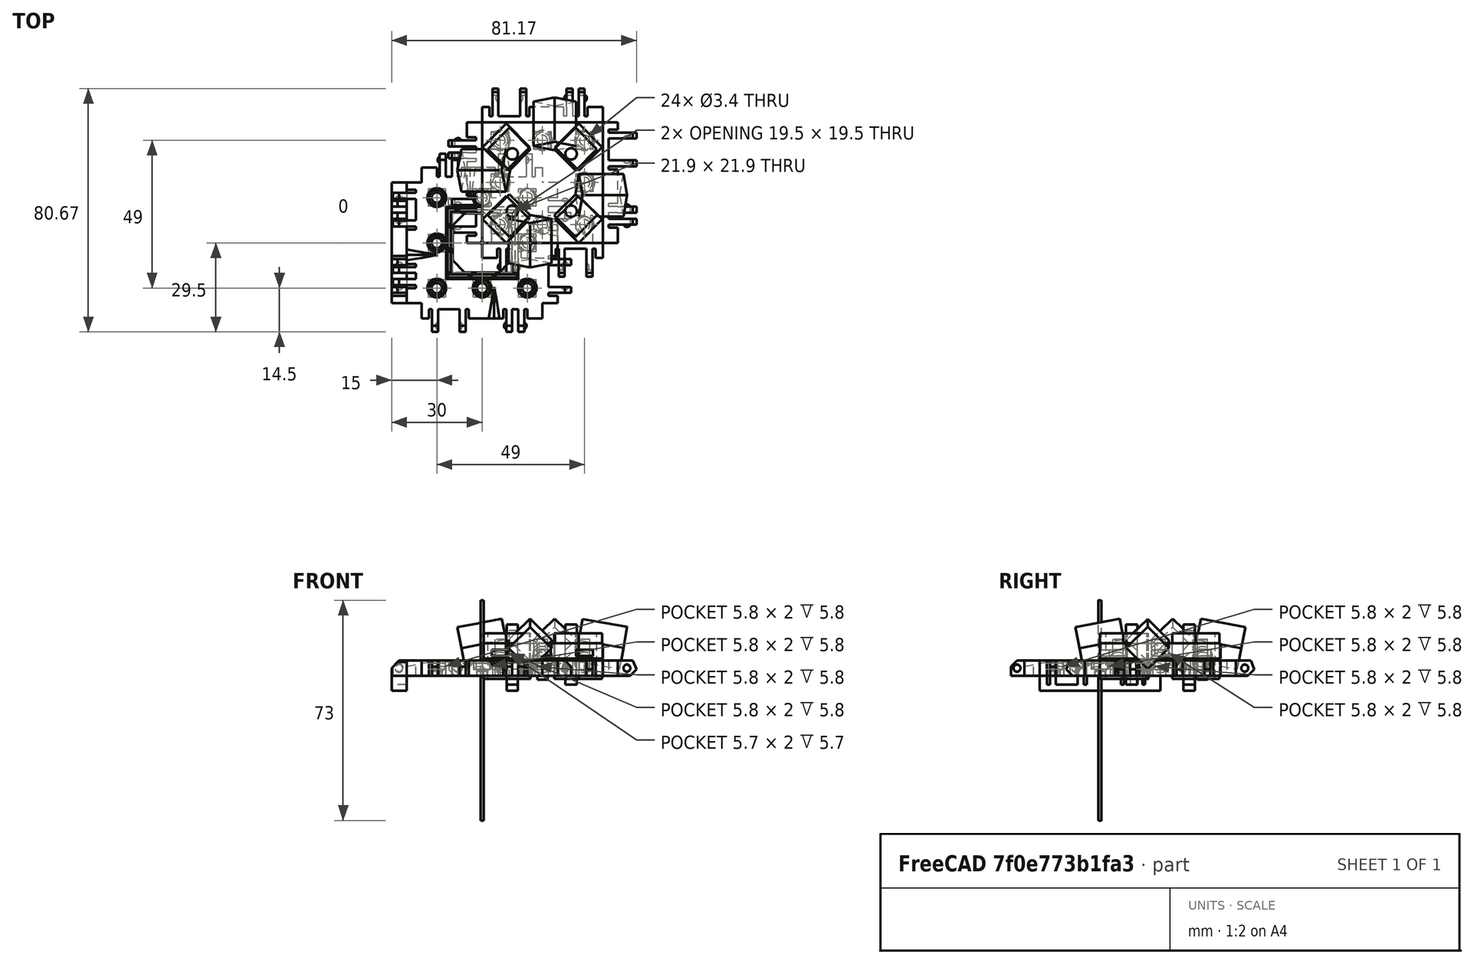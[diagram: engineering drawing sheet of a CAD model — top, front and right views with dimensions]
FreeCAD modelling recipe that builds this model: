
FCSTD DOCUMENT  (FreeCAD 0.17R13522 (Git))
Label: Robot Plates 1.1
License: All rights reserved
LicenseURL: http://en.wikipedia.org/wiki/All_rights_reserved
objects: Part::Box×265, Part::Cut×90, Part::Sphere×89, Part::MultiFuse×64, Part::Cylinder×34, Part::Fuse×30, Part::Chamfer×11, Drawing::FeatureViewAnnotation×7, App::DocumentObjectGroup×3, Part::Feature×3, Drawing::FeaturePage×2
note: 586 computed .brp shape members not serialized (recipe doc carries the construction recipe); baked Part::Feature solids carry a one-line shape summary decoded from their .brp

FEATURE [Part::Box] Box  label="Cube"
  AttacherType = Attacher::AttachEngine3D
  Height = 5
  Length = 40
  Placement = pos=(-20,-20,-2) rot=(0,0,1;0rad)
  Width = 40
FEATURE [Part::Sphere] Sphere003  label="Mag Hole 3"
  Angle1 = -90
  Angle2 = 90
  Angle3 = 360
  AttacherType = Attacher::AttachEngine3D
  Placement = pos=(-15,15,1.7) rot=(0,0,1;0rad)
  Radius = 2.83
FEATURE [Part::Sphere] Sphere005  label="Mag Hole 2"
  Angle1 = -90
  Angle2 = 90
  Angle3 = 360
  AttacherType = Attacher::AttachEngine3D
  Placement = pos=(15,0,1.7) rot=(0,0,1;0rad)
  Radius = 2.825
FEATURE [Part::Sphere] Sphere  label="Mag Hole"
  Angle1 = -90
  Angle2 = 90
  Angle3 = 360
  AttacherType = Attacher::AttachEngine3D
  Placement = pos=(-15,-15,1.7) rot=(0,0,1;0rad)
  Radius = 2.83
FEATURE [Part::MultiFuse] Fusion004  label="Ball Holes"
  Shapes = -> [Sphere,Sphere005,Sphere003]
FEATURE [Part::Cut] Cut003
  Base = -> Box
  Tool = -> Fusion004
FEATURE [Part::Box] Box001  label="Cube001"
  AttacherType = Attacher::AttachEngine3D
  Height = 7
  Length = 5
  Placement = pos=(-5,0,-2) rot=(0,0,1;0rad)
  Width = 40
FEATURE [Part::Box] Box002  label="Cube002"
  AttacherType = Attacher::AttachEngine3D
  Height = 7
  Length = 10
  Placement = pos=(-15,6,-2) rot=(0,0,1;0rad)
  Width = 2
FEATURE [Part::Box] Box003  label="Cube003"
  AttacherType = Attacher::AttachEngine3D
  Height = 7
  Length = 10
  Placement = pos=(-15,10,-2) rot=(0,0,1;0rad)
  Width = 2
FEATURE [Part::Box] Box004  label="Cube004"
  AttacherType = Attacher::AttachEngine3D
  Height = 7
  Length = 10
  Placement = pos=(-15,25.4,-2) rot=(0,0,1;0rad)
  Width = 2
FEATURE [Part::Box] Box005  label="Cube005"
  AttacherType = Attacher::AttachEngine3D
  Height = 7
  Length = 10
  Placement = pos=(-15,34.6,-2) rot=(0,0,1;0rad)
  Width = 2
FEATURE [Part::Sphere] Sphere008
  Angle1 = -90
  Angle2 = 90
  Angle3 = 360
  AttacherType = Attacher::AttachEngine3D
  Placement = pos=(-7.5,6.5,0.5) rot=(0,0,1;0rad)
  Radius = 1.25
FEATURE [Part::Box] Box006  label="Chamfer Cube"
  AttacherType = Attacher::AttachEngine3D
  Height = 10
  Length = 13
  Placement = pos=(-11.69,0,-1.19) rot=(0,-1,0;0.785398rad)
  Width = 40
FEATURE [Part::Sphere] Sphere009
  Angle1 = -90
  Angle2 = 90
  Angle3 = 360
  AttacherType = Attacher::AttachEngine3D
  Placement = pos=(-7.5,11.5,0.5) rot=(0,0,1;0rad)
  Radius = 1.25
FEATURE [Part::Sphere] Sphere010
  Angle1 = -90
  Angle2 = 90
  Angle3 = 360
  AttacherType = Attacher::AttachEngine3D
  Placement = pos=(-7.5,28,0.5) rot=(0,0,1;0rad)
  Radius = 1.5
FEATURE [Part::Sphere] Sphere011
  Angle1 = -90
  Angle2 = 90
  Angle3 = 360
  AttacherType = Attacher::AttachEngine3D
  Placement = pos=(-7.5,34,0.5) rot=(0,0,1;0rad)
  Radius = 1.5
FEATURE [Part::Box] Box007  label="Cube007"
  AttacherType = Attacher::AttachEngine3D
  Height = 7
  Length = 4
  Placement = pos=(-6,5,-2) rot=(0,0,1;0rad)
  Width = 1
FEATURE [Part::Box] Box008  label="Cube008"
  AttacherType = Attacher::AttachEngine3D
  Height = 7
  Length = 4
  Placement = pos=(-6,8,-2) rot=(0,0,1;0rad)
  Width = 2
FEATURE [Part::Box] Box009  label="Cube009"
  AttacherType = Attacher::AttachEngine3D
  Height = 7
  Length = 4
  Placement = pos=(-6,12,-2) rot=(0,0,1;0rad)
  Width = 1
FEATURE [Part::Box] Box010  label="Cube010"
  AttacherType = Attacher::AttachEngine3D
  Height = 7
  Length = 4
  Placement = pos=(-6,24.4,-2) rot=(0,0,1;0rad)
  Width = 1
FEATURE [Part::Box] Box011  label="Cube011"
  AttacherType = Attacher::AttachEngine3D
  Height = 7
  Length = 4
  Placement = pos=(-6,36.6,-2) rot=(0,0,1;0rad)
  Width = 1
FEATURE [Part::Box] Box012  label="Cube012"
  AttacherType = Attacher::AttachEngine3D
  Height = 7
  Length = 4
  Placement = pos=(-6,27.4,-2) rot=(0,0,1;0rad)
  Width = 7.2
FEATURE [Part::MultiFuse] Fusion003  label="Extra Holes for Clips"
  Shapes = -> [Box012,Box009,Box011,Box008,Box010,Box007]
FEATURE [Part::Box] Box013  label="Re-level Edge Clip Block"
  AttacherType = Attacher::AttachEngine3D
  Height = 10
  Length = 20
  Placement = pos=(-19,-2,3) rot=(0,0,1;0rad)
  Width = 44
FEATURE [Part::Box] Box014  label="Cube014"
  AttacherType = Attacher::AttachEngine3D
  Height = 7
  Length = 10
  Placement = pos=(-10,34.6,0) rot=(0,0,1;0rad)
  Width = 2
FEATURE [Part::Box] Box015  label="Cube015"
  AttacherType = Attacher::AttachEngine3D
  Height = 7
  Length = 5
  Width = 40
FEATURE [Part::Box] Box016  label="Cube016"
  AttacherType = Attacher::AttachEngine3D
  Height = 7
  Length = 10
  Placement = pos=(-10,25.4,0) rot=(0,0,1;0rad)
  Width = 2
FEATURE [Part::Box] Box017  label="Cube017"
  AttacherType = Attacher::AttachEngine3D
  Height = 7
  Length = 10
  Placement = pos=(-10,10,0) rot=(0,0,1;0rad)
  Width = 2
FEATURE [Part::Box] Box018  label="Cube018"
  AttacherType = Attacher::AttachEngine3D
  Height = 7
  Length = 10
  Placement = pos=(-10,6,0) rot=(0,0,1;0rad)
  Width = 2
FEATURE [Part::Sphere] Sphere012
  Angle1 = -90
  Angle2 = 90
  Angle3 = 360
  AttacherType = Attacher::AttachEngine3D
  Placement = pos=(-3,6.5,2.5) rot=(0,0,1;0rad)
  Radius = 1.25
FEATURE [Part::Box] Box019  label="Cube019"
  AttacherType = Attacher::AttachEngine3D
  Height = 10
  Length = 13
  Placement = pos=(-10.19,0,-1.19) rot=(0,-1,0;0.785398rad)
  Width = 40
FEATURE [Part::Sphere] Sphere013
  Angle1 = -90
  Angle2 = 90
  Angle3 = 360
  AttacherType = Attacher::AttachEngine3D
  Placement = pos=(-3,11.5,2.5) rot=(0,0,1;0rad)
  Radius = 1.25
FEATURE [Part::Sphere] Sphere014
  Angle1 = -90
  Angle2 = 90
  Angle3 = 360
  AttacherType = Attacher::AttachEngine3D
  Placement = pos=(-3,28,2.5) rot=(0,0,1;0rad)
  Radius = 1.5
FEATURE [Part::Sphere] Sphere015
  Angle1 = -90
  Angle2 = 90
  Angle3 = 360
  AttacherType = Attacher::AttachEngine3D
  Placement = pos=(-3,34,2.5) rot=(0,0,1;0rad)
  Radius = 1.5
FEATURE [Part::MultiFuse] Fusion005
  Shapes = -> [Box015,Box018,Box017,Box016,Box014]
FEATURE [Part::Cut] Cut005
  Base = -> Fusion005
  Tool = -> Box019
FEATURE [Part::MultiFuse] Fusion006
  Shapes = -> [Sphere012,Sphere013,Cut005]
FEATURE [Part::MultiFuse] Fusion007
  Shapes = -> [Sphere015,Sphere014]
FEATURE [Part::Cut] Cut006
  Base = -> Fusion006
  Tool = -> Fusion007
FEATURE [Part::Chamfer] Chamfer002
  Base = -> Cut006
  Edges = 4 edges r=4: [Edge31,Edge37,Edge43,Edge46]
FEATURE [Part::Box] Box020  label="Cube020"
  AttacherType = Attacher::AttachEngine3D
  Height = 7
  Length = 4
  Placement = pos=(-1,5,0) rot=(0,0,1;0rad)
  Width = 1
FEATURE [Part::Box] Box021  label="Cube021"
  AttacherType = Attacher::AttachEngine3D
  Height = 7
  Length = 4
  Placement = pos=(-1,8,0) rot=(0,0,1;0rad)
  Width = 2
FEATURE [Part::Box] Box022  label="Cube022"
  AttacherType = Attacher::AttachEngine3D
  Height = 7
  Length = 4
  Placement = pos=(-1,12,0) rot=(0,0,1;0rad)
  Width = 1
FEATURE [Part::Box] Box023  label="Cube023"
  AttacherType = Attacher::AttachEngine3D
  Height = 7
  Length = 4
  Placement = pos=(-1,24.4,0) rot=(0,0,1;0rad)
  Width = 1
FEATURE [Part::Box] Box024  label="Cube024"
  AttacherType = Attacher::AttachEngine3D
  Height = 7
  Length = 4
  Placement = pos=(-1,36.6,0) rot=(0,0,1;0rad)
  Width = 1
FEATURE [Part::Box] Box025  label="Cube025"
  AttacherType = Attacher::AttachEngine3D
  Height = 7
  Length = 4
  Placement = pos=(-1,27.4,0) rot=(0,0,1;0rad)
  Width = 7.2
FEATURE [Part::MultiFuse] Fusion008
  Shapes = -> [Box025,Box022,Box024,Box021,Box023,Box020]
FEATURE [Part::Cut] Cut007
  Base = -> Chamfer002
  Placement = pos=(-5,40,3) rot=(1,0,0;3.14159rad)
  Tool = -> Fusion008
FEATURE [Part::Box] Box026  label="Cube026"
  AttacherType = Attacher::AttachEngine3D
  Height = 10
  Length = 12
  Placement = pos=(-11,-2,-12) rot=(0,0,1;0rad)
  Width = 44
FEATURE [Part::Cut] Cut008
  Base = -> Cut007
  Placement = pos=(40,0,0) rot=(0,0,1;1.5708rad)
  Tool = -> Box026
FEATURE [Part::Box] Box027  label="Cube027"
  AttacherType = Attacher::AttachEngine3D
  Height = 7
  Length = 4
  Placement = pos=(-1,12,0) rot=(0,0,1;0rad)
  Width = 1
FEATURE [Part::Box] Box028  label="Cube028"
  AttacherType = Attacher::AttachEngine3D
  Height = 10
  Length = 13
  Placement = pos=(-10.19,0,-1.19) rot=(0,-1,0;0.785398rad)
  Width = 40
FEATURE [Part::Box] Box029  label="Cube029"
  AttacherType = Attacher::AttachEngine3D
  Height = 7
  Length = 4
  Placement = pos=(-1,27.4,0) rot=(0,0,1;0rad)
  Width = 7.2
FEATURE [Part::Box] Box030  label="Cube030"
  AttacherType = Attacher::AttachEngine3D
  Height = 7
  Length = 4
  Placement = pos=(-1,5,0) rot=(0,0,1;0rad)
  Width = 1
FEATURE [Part::Box] Box031  label="Cube031"
  AttacherType = Attacher::AttachEngine3D
  Height = 7
  Length = 10
  Placement = pos=(-10,6,0) rot=(0,0,1;0rad)
  Width = 2
FEATURE [Part::Box] Box032  label="Cube032"
  AttacherType = Attacher::AttachEngine3D
  Height = 10
  Length = 12
  Placement = pos=(-11,-2,-12) rot=(0,0,1;0rad)
  Width = 44
FEATURE [Part::Sphere] Sphere016
  Angle1 = -90
  Angle2 = 90
  Angle3 = 360
  AttacherType = Attacher::AttachEngine3D
  Placement = pos=(-3,6.5,2.5) rot=(0,0,1;0rad)
  Radius = 1.25
FEATURE [Part::Box] Box033  label="Cube033"
  AttacherType = Attacher::AttachEngine3D
  Height = 7
  Length = 10
  Placement = pos=(-10,25.4,0) rot=(0,0,1;0rad)
  Width = 2
FEATURE [Part::Box] Box034  label="Cube034"
  AttacherType = Attacher::AttachEngine3D
  Height = 7
  Length = 10
  Placement = pos=(-10,10,0) rot=(0,0,1;0rad)
  Width = 2
FEATURE [Part::Sphere] Sphere017
  Angle1 = -90
  Angle2 = 90
  Angle3 = 360
  AttacherType = Attacher::AttachEngine3D
  Placement = pos=(-3,28,2.5) rot=(0,0,1;0rad)
  Radius = 1.5
FEATURE [Part::Sphere] Sphere018
  Angle1 = -90
  Angle2 = 90
  Angle3 = 360
  AttacherType = Attacher::AttachEngine3D
  Placement = pos=(-3,11.5,2.5) rot=(0,0,1;0rad)
  Radius = 1.25
FEATURE [Part::Box] Box035  label="Cube035"
  AttacherType = Attacher::AttachEngine3D
  Height = 7
  Length = 4
  Placement = pos=(-1,36.6,0) rot=(0,0,1;0rad)
  Width = 1
FEATURE [Part::Sphere] Sphere019
  Angle1 = -90
  Angle2 = 90
  Angle3 = 360
  AttacherType = Attacher::AttachEngine3D
  Placement = pos=(-3,34,2.5) rot=(0,0,1;0rad)
  Radius = 1.5
FEATURE [Part::MultiFuse] Fusion011
  Shapes = -> [Sphere019,Sphere017]
FEATURE [Part::Box] Box036  label="Cube036"
  AttacherType = Attacher::AttachEngine3D
  Height = 7
  Length = 4
  Placement = pos=(-1,8,0) rot=(0,0,1;0rad)
  Width = 2
FEATURE [Part::Box] Box037  label="Cube037"
  AttacherType = Attacher::AttachEngine3D
  Height = 7
  Length = 10
  Placement = pos=(-10,34.6,0) rot=(0,0,1;0rad)
  Width = 2
FEATURE [Part::Box] Box038  label="Cube038"
  AttacherType = Attacher::AttachEngine3D
  Height = 7
  Length = 4
  Placement = pos=(-1,24.4,0) rot=(0,0,1;0rad)
  Width = 1
FEATURE [Part::MultiFuse] Fusion009
  Shapes = -> [Box029,Box027,Box035,Box036,Box038,Box030]
FEATURE [Part::Box] Box039  label="Cube039"
  AttacherType = Attacher::AttachEngine3D
  Height = 7
  Length = 5
  Width = 40
FEATURE [Part::MultiFuse] Fusion012
  Shapes = -> [Box039,Box031,Box034,Box033,Box037]
FEATURE [Part::Cut] Cut011
  Base = -> Fusion012
  Tool = -> Box028
FEATURE [Part::MultiFuse] Fusion010
  Shapes = -> [Sphere016,Sphere018,Cut011]
FEATURE [Part::Cut] Cut012
  Base = -> Fusion010
  Tool = -> Fusion011
FEATURE [Part::Chamfer] Chamfer003
  Base = -> Cut012
  Edges = 4 edges r=4: [Edge31,Edge37,Edge43,Edge46]
FEATURE [Part::Cut] Cut010
  Base = -> Chamfer003
  Placement = pos=(-5,40,3) rot=(1,0,0;3.14159rad)
  Tool = -> Fusion009
FEATURE [Part::Cut] Cut009
  Base = -> Cut010
  Placement = pos=(40,40,0) rot=(0,0,1;3.14159rad)
  Tool = -> Box032
FEATURE [Part::Sphere] Sphere020
  Angle1 = -90
  Angle2 = 90
  Angle3 = 360
  AttacherType = Attacher::AttachEngine3D
  Placement = pos=(-3,11.5,2.5) rot=(0,0,1;0rad)
  Radius = 1.25
FEATURE [Part::Box] Box040  label="Cube040"
  AttacherType = Attacher::AttachEngine3D
  Height = 7
  Length = 10
  Placement = pos=(-10,6,0) rot=(0,0,1;0rad)
  Width = 2
FEATURE [Part::Box] Box041  label="Cube041"
  AttacherType = Attacher::AttachEngine3D
  Height = 7
  Length = 4
  Placement = pos=(-1,8,0) rot=(0,0,1;0rad)
  Width = 2
FEATURE [Part::Box] Box042  label="Cube042"
  AttacherType = Attacher::AttachEngine3D
  Height = 7
  Length = 10
  Placement = pos=(-10,10,0) rot=(0,0,1;0rad)
  Width = 2
FEATURE [Part::Box] Box043  label="Cube043"
  AttacherType = Attacher::AttachEngine3D
  Height = 10
  Length = 12
  Placement = pos=(-11,-2,-12) rot=(0,0,1;0rad)
  Width = 44
FEATURE [Part::Box] Box044  label="Cube044"
  AttacherType = Attacher::AttachEngine3D
  Height = 7
  Length = 4
  Placement = pos=(-1,5,0) rot=(0,0,1;0rad)
  Width = 1
FEATURE [Part::Sphere] Sphere021
  Angle1 = -90
  Angle2 = 90
  Angle3 = 360
  AttacherType = Attacher::AttachEngine3D
  Placement = pos=(-3,28,2.5) rot=(0,0,1;0rad)
  Radius = 1.5
FEATURE [Part::Sphere] Sphere022
  Angle1 = -90
  Angle2 = 90
  Angle3 = 360
  AttacherType = Attacher::AttachEngine3D
  Placement = pos=(-3,6.5,2.5) rot=(0,0,1;0rad)
  Radius = 1.25
FEATURE [Part::Sphere] Sphere023
  Angle1 = -90
  Angle2 = 90
  Angle3 = 360
  AttacherType = Attacher::AttachEngine3D
  Placement = pos=(-3,34,2.5) rot=(0,0,1;0rad)
  Radius = 1.5
FEATURE [Part::Box] Box045  label="Cube045"
  AttacherType = Attacher::AttachEngine3D
  Height = 7
  Length = 4
  Placement = pos=(-1,12,0) rot=(0,0,1;0rad)
  Width = 1
FEATURE [Part::Box] Box046  label="Cube046"
  AttacherType = Attacher::AttachEngine3D
  Height = 7
  Length = 5
  Width = 40
FEATURE [Part::Box] Box047  label="Cube047"
  AttacherType = Attacher::AttachEngine3D
  Height = 7
  Length = 4
  Placement = pos=(-1,36.6,0) rot=(0,0,1;0rad)
  Width = 1
FEATURE [Part::Box] Box048  label="Cube048"
  AttacherType = Attacher::AttachEngine3D
  Height = 7
  Length = 4
  Placement = pos=(-1,24.4,0) rot=(0,0,1;0rad)
  Width = 1
FEATURE [Part::Box] Box049  label="Cube049"
  AttacherType = Attacher::AttachEngine3D
  Height = 7
  Length = 10
  Placement = pos=(-10,25.4,0) rot=(0,0,1;0rad)
  Width = 2
FEATURE [Part::Box] Box050  label="Cube050"
  AttacherType = Attacher::AttachEngine3D
  Height = 10
  Length = 13
  Placement = pos=(-10.19,0,-1.19) rot=(0,-1,0;0.785398rad)
  Width = 40
FEATURE [Part::Box] Box051  label="Cube051"
  AttacherType = Attacher::AttachEngine3D
  Height = 7
  Length = 10
  Placement = pos=(-10,34.6,0) rot=(0,0,1;0rad)
  Width = 2
FEATURE [Part::MultiFuse] Fusion015
  Shapes = -> [Box046,Box040,Box042,Box049,Box051]
FEATURE [Part::Cut] Cut013
  Base = -> Fusion015
  Tool = -> Box050
FEATURE [Part::MultiFuse] Fusion013
  Shapes = -> [Sphere022,Sphere020,Cut013]
FEATURE [Part::MultiFuse] Fusion016
  Shapes = -> [Sphere023,Sphere021]
FEATURE [Part::Cut] Cut014
  Base = -> Fusion013
  Tool = -> Fusion016
FEATURE [Part::Chamfer] Chamfer004
  Base = -> Cut014
  Edges = 4 edges r=4: [Edge31,Edge37,Edge43,Edge46]
FEATURE [Part::Box] Box052  label="Cube052"
  AttacherType = Attacher::AttachEngine3D
  Height = 7
  Length = 4
  Placement = pos=(-1,27.4,0) rot=(0,0,1;0rad)
  Width = 7.2
FEATURE [Part::MultiFuse] Fusion014
  Shapes = -> [Box052,Box045,Box047,Box041,Box048,Box044]
FEATURE [Part::Cut] Cut016
  Base = -> Chamfer004
  Placement = pos=(-5,40,3) rot=(1,0,0;3.14159rad)
  Tool = -> Fusion014
FEATURE [Part::Cut] Cut015
  Base = -> Cut016
  Placement = pos=(0,40,0) rot=(0,0,-1;1.5708rad)
  Tool = -> Box043
FEATURE [Part::Box] Box054  label="Cube054"
  AttacherType = Attacher::AttachEngine3D
  Height = 15
  Length = 10
  Placement = pos=(9,2,-3) rot=(0,0,1;0.785398rad)
  Width = 10
FEATURE [Part::Box] Box055  label="Cube055"
  AttacherType = Attacher::AttachEngine3D
  Height = 15
  Length = 10
  Placement = pos=(31,24,-3) rot=(0,0,1;0.785398rad)
  Width = 10
FEATURE [Part::Box] Box056  label="Cube056"
  AttacherType = Attacher::AttachEngine3D
  Height = 15
  Length = 10
  Placement = pos=(31,2,-3) rot=(0,0,1;0.785398rad)
  Width = 10
FEATURE [Part::Box] Box057  label="Cube057"
  AttacherType = Attacher::AttachEngine3D
  Height = 15
  Length = 10
  Placement = pos=(9,24,-3) rot=(0,0,1;0.785398rad)
  Width = 10
FEATURE [Part::MultiFuse] Fusion017
  Shapes = -> [Box054,Box057,Box056,Box055]
FEATURE [Part::Box] Box058  label="Cube058"
  AttacherType = Attacher::AttachEngine3D
  Height = 5
  Length = 40
  Placement = pos=(0,0,3.7) rot=(0,0,1;0rad)
  Width = 40
FEATURE [Part::Box] Box059  label="Square Nut Hole 008"
  AttacherType = Attacher::AttachEngine3D
  Height = 2
  Length = 5.6
  Placement = pos=(17.2,31.2,4.6) rot=(0,0,1;0rad)
  Width = 5.6
FEATURE [Part::Box] Box060  label="Square Nut Hole 009"
  AttacherType = Attacher::AttachEngine3D
  Height = 2
  Length = 5.6
  Placement = pos=(17.2,-0.85,4.6) rot=(0,0,1;0rad)
  Width = 10
FEATURE [Part::Box] Box061  label="Square Nut Hole 010"
  AttacherType = Attacher::AttachEngine3D
  Height = 2
  Length = 5.6
  Placement = pos=(31.2,-0.85,4.6) rot=(0,0,1;0rad)
  Width = 10
FEATURE [Part::Box] Box062  label="Square Nut Hole 011"
  AttacherType = Attacher::AttachEngine3D
  Height = 2
  Length = 5.4
  Placement = pos=(31.3,17.3,4.6) rot=(0,0,1;0rad)
  Width = 5.4
FEATURE [Part::Box] Box063  label="Square Nut Hole 012"
  AttacherType = Attacher::AttachEngine3D
  Height = 2
  Length = 5.7
  Placement = pos=(3.15,31.15,4.6) rot=(0,0,1;0rad)
  Width = 5.7
FEATURE [Part::Box] Box064  label="Square Nut Hole 013"
  AttacherType = Attacher::AttachEngine3D
  Height = 2
  Length = 5.5
  Placement = pos=(31.25,31.25,4.6) rot=(0,0,1;0rad)
  Width = 5.5
FEATURE [Part::Box] Box065  label="Square Nut Hole 014"
  AttacherType = Attacher::AttachEngine3D
  Height = 2
  Length = 5.8
  Placement = pos=(3.1,17.1,4.6) rot=(0,0,1;0rad)
  Width = 5.8
FEATURE [Part::Box] Box066  label="Square Nut Hole 015"
  AttacherType = Attacher::AttachEngine3D
  Height = 2
  Length = 5.6
  Placement = pos=(3.2,-0.85,4.6) rot=(0,0,1;0rad)
  Width = 10
FEATURE [Part::Sphere] Sphere006  label="Nut Clearence1"
  Angle1 = -90
  Angle2 = 90
  Angle3 = 360
  AttacherType = Attacher::AttachEngine3D
  Placement = pos=(6,6,2.4) rot=(0,0,1;0rad)
  Radius = 3.35
FEATURE [Part::Sphere] Sphere024
  Angle1 = -90
  Angle2 = 90
  Angle3 = 360
  AttacherType = Attacher::AttachEngine3D
  Placement = pos=(6,34,2.4) rot=(0,0,1;0rad)
  Radius = 3.35
FEATURE [Part::Sphere] Sphere007
  Angle1 = -90
  Angle2 = 90
  Angle3 = 360
  AttacherType = Attacher::AttachEngine3D
  Placement = pos=(34,20,2.4) rot=(0,0,1;0rad)
  Radius = 3.35
FEATURE [Part::Sphere] Sphere001
  Angle1 = -90
  Angle2 = 90
  Angle3 = 360
  AttacherType = Attacher::AttachEngine3D
  Placement = pos=(34,6,2.4) rot=(0,0,1;0rad)
  Radius = 3.35
FEATURE [Part::Sphere] Sphere025
  Angle1 = -90
  Angle2 = 90
  Angle3 = 360
  AttacherType = Attacher::AttachEngine3D
  Placement = pos=(20,6,2.4) rot=(0,0,1;0rad)
  Radius = 3.35
FEATURE [Part::Sphere] Sphere026
  Angle1 = -90
  Angle2 = 90
  Angle3 = 360
  AttacherType = Attacher::AttachEngine3D
  Placement = pos=(20,34,2.4) rot=(0,0,1;0rad)
  Radius = 3.35
FEATURE [Part::Sphere] Sphere004
  Angle1 = -90
  Angle2 = 90
  Angle3 = 360
  AttacherType = Attacher::AttachEngine3D
  Placement = pos=(6,20,2.4) rot=(0,0,1;0rad)
  Radius = 3.35
FEATURE [Part::Sphere] Sphere002
  Angle1 = -90
  Angle2 = 90
  Angle3 = 360
  AttacherType = Attacher::AttachEngine3D
  Placement = pos=(34,34,2.4) rot=(0,0,1;0rad)
  Radius = 3.35
FEATURE [Part::Cylinder] Cylinder
  Angle = 360
  AttacherType = Attacher::AttachEngine3D
  Height = 10
  Placement = pos=(6,6,0) rot=(0,0,1;0rad)
  Radius = 1.7
FEATURE [Part::Cylinder] Cylinder002
  Angle = 360
  AttacherType = Attacher::AttachEngine3D
  Height = 10
  Placement = pos=(34,6,0) rot=(0,0,1;0rad)
  Radius = 1.7
FEATURE [Part::Cylinder] Cylinder001
  Angle = 360
  AttacherType = Attacher::AttachEngine3D
  Height = 10
  Placement = pos=(20,6,0) rot=(0,0,1;0rad)
  Radius = 1.7
FEATURE [Part::Cylinder] Cylinder003
  Angle = 360
  AttacherType = Attacher::AttachEngine3D
  Height = 10
  Placement = pos=(34,34,0) rot=(0,0,1;0rad)
  Radius = 1.7
FEATURE [Part::Cylinder] Cylinder004
  Angle = 360
  AttacherType = Attacher::AttachEngine3D
  Height = 10
  Placement = pos=(20,34,0) rot=(0,0,1;0rad)
  Radius = 1.7
FEATURE [Part::Cylinder] Cylinder005
  Angle = 360
  AttacherType = Attacher::AttachEngine3D
  Height = 10
  Placement = pos=(6,34,0) rot=(0,0,1;0rad)
  Radius = 1.7
FEATURE [Part::Cylinder] Cylinder006
  Angle = 360
  AttacherType = Attacher::AttachEngine3D
  Height = 10
  Placement = pos=(6,20,0) rot=(0,0,1;0rad)
  Radius = 1.7
FEATURE [Part::Cylinder] Cylinder007
  Angle = 360
  AttacherType = Attacher::AttachEngine3D
  Height = 10
  Placement = pos=(34,20,0) rot=(0,0,1;0rad)
  Radius = 1.7
FEATURE [Part::MultiFuse] Fusion018
  Shapes = -> [Cylinder,Cylinder004,Cylinder007,Cylinder005,Cylinder006,Cylinder001,Cylinder002,Cylinder003]
FEATURE [Part::MultiFuse] Fusion019
  Shapes = -> [Sphere007,Sphere024,Sphere006,Sphere025,Sphere001,Sphere026,Sphere004,Sphere002]
FEATURE [Part::MultiFuse] Fusion020
  Shapes = -> [Box061,Box065,Box062,Box063,Box064,Box066,Box059,Box060]
FEATURE [Part::Cut] Cut017
  Base = -> Box058
  Tool = -> Fusion020
FEATURE [Part::Cut] Cut019
  Base = -> Cut017
  Tool = -> Fusion019
FEATURE [Part::Cut] Cut018
  Base = -> Cut019
  Tool = -> Fusion018
FEATURE [Part::Cylinder] Cylinder008
  Angle = 360
  AttacherType = Attacher::AttachEngine3D
  Height = 20
  Placement = pos=(10,10.5,-5) rot=(0,0,1;0rad)
  Radius = 1.9
FEATURE [Part::Cylinder] Cylinder009
  Angle = 360
  AttacherType = Attacher::AttachEngine3D
  Height = 20
  Placement = pos=(29.5,10.5,-5) rot=(0,0,1;0rad)
  Radius = 1.9
FEATURE [Part::Cylinder] Cylinder010
  Angle = 360
  AttacherType = Attacher::AttachEngine3D
  Height = 20
  Placement = pos=(29.5,29.5,-5) rot=(0,0,1;0rad)
  Radius = 1.9
FEATURE [Part::Cylinder] Cylinder011
  Angle = 360
  AttacherType = Attacher::AttachEngine3D
  Height = 20
  Placement = pos=(10,29.5,-7) rot=(0,0,1;0rad)
  Radius = 1.9
FEATURE [Part::MultiFuse] Fusion021  label="M2 Screw holes"
  Shapes = -> [Cylinder008,Cylinder009,Cylinder011,Cylinder010]
FEATURE [Part::Box] Box067  label="Square Nut Hole 016"
  AttacherType = Attacher::AttachEngine3D
  Height = 2
  Length = 5.8
  Placement = pos=(31.1,17.1,4.6) rot=(0,0,1;0rad)
  Width = 5.8
FEATURE [Part::Box] Box068  label="Square Nut Hole 017"
  AttacherType = Attacher::AttachEngine3D
  Height = 2
  Length = 5.8
  Placement = pos=(17.1,36.9,2.1) rot=(1,0,0;3.14159rad)
  Width = 5.8
FEATURE [Part::Box] Box069  label="Square Nut Hole 018"
  AttacherType = Attacher::AttachEngine3D
  Height = 2
  Length = 5.8
  Placement = pos=(-2.9,2.9,2.1) rot=(1,0,0;3.14159rad)
  Width = 5.8
FEATURE [Part::Box] Box070  label="Square Nut Hole 019"
  AttacherType = Attacher::AttachEngine3D
  Height = 2
  Length = 5.8
  Placement = pos=(3.1,3.1,4.6) rot=(0,0,1;0rad)
  Width = 5.8
FEATURE [Part::Box] Box071  label="Square Nut Hole 020"
  AttacherType = Attacher::AttachEngine3D
  Height = 2
  Length = 5.8
  Placement = pos=(3.1,31.1,4.6) rot=(0,0,1;0rad)
  Width = 5.8
FEATURE [Part::Box] Box072  label="Square Nut Hole 021"
  AttacherType = Attacher::AttachEngine3D
  Height = 2
  Length = 5.8
  Placement = pos=(17.1,31.1,4.6) rot=(0,0,1;0rad)
  Width = 5.8
FEATURE [Part::Box] Box073  label="Square Nut Hole 022"
  AttacherType = Attacher::AttachEngine3D
  Height = 2
  Length = 5.8
  Placement = pos=(31.1,31.1,4.6) rot=(0,0,1;0rad)
  Width = 5.8
FEATURE [Part::Box] Box074  label="Square Nut Hole 023"
  AttacherType = Attacher::AttachEngine3D
  Height = 2
  Length = 5.8
  Placement = pos=(3.1,17.1,4.6) rot=(0,0,1;0rad)
  Width = 5.8
FEATURE [Part::Cylinder] Cylinder012
  Angle = 360
  AttacherType = Attacher::AttachEngine3D
  Height = 10
  Placement = pos=(6,6,0) rot=(0,0,1;0rad)
  Radius = 1.7
FEATURE [Part::Cylinder] Cylinder013
  Angle = 360
  AttacherType = Attacher::AttachEngine3D
  Height = 10
  Placement = pos=(34,34,0) rot=(0,0,1;0rad)
  Radius = 1.7
FEATURE [Part::Cylinder] Cylinder014
  Angle = 360
  AttacherType = Attacher::AttachEngine3D
  Height = 10
  Placement = pos=(20,34,0) rot=(0,0,1;0rad)
  Radius = 1.7
FEATURE [Part::Cylinder] Cylinder015
  Angle = 360
  AttacherType = Attacher::AttachEngine3D
  Height = 10
  Placement = pos=(6,34,0) rot=(0,0,1;0rad)
  Radius = 1.7
FEATURE [Part::Cylinder] Cylinder016
  Angle = 360
  AttacherType = Attacher::AttachEngine3D
  Height = 10
  Placement = pos=(6,20,0) rot=(0,0,1;0rad)
  Radius = 1.7
FEATURE [Part::Cylinder] Cylinder017
  Angle = 360
  AttacherType = Attacher::AttachEngine3D
  Height = 10
  Placement = pos=(34,20,0) rot=(0,0,1;0rad)
  Radius = 1.7
FEATURE [Part::Cylinder] Cylinder018
  Angle = 360
  AttacherType = Attacher::AttachEngine3D
  Height = 10
  Placement = pos=(0,0,6.7) rot=(1,0,0;3.14159rad)
  Radius = 1.7
FEATURE [Part::Cylinder] Cylinder019
  Angle = 360
  AttacherType = Attacher::AttachEngine3D
  Height = 10
  Placement = pos=(20,34,6.7) rot=(1,0,0;3.14159rad)
  Radius = 1.7
FEATURE [Part::Box] Box075  label="Cube059"
  AttacherType = Attacher::AttachEngine3D
  Height = 5
  Length = 40
  Placement = pos=(-20,-20,-2) rot=(0,0,1;0rad)
  Width = 40
FEATURE [Part::Sphere] Sphere027
  Angle1 = -90
  Angle2 = 90
  Angle3 = 360
  AttacherType = Attacher::AttachEngine3D
  Placement = pos=(34,20,2.4) rot=(0,0,1;0rad)
  Radius = 3.35
FEATURE [Part::Sphere] Sphere028  label="Nut Clearence002"
  Angle1 = -90
  Angle2 = 90
  Angle3 = 360
  AttacherType = Attacher::AttachEngine3D
  Placement = pos=(6,6,2.4) rot=(0,0,1;0rad)
  Radius = 3.35
FEATURE [Part::Sphere] Sphere029
  Angle1 = -90
  Angle2 = 90
  Angle3 = 360
  AttacherType = Attacher::AttachEngine3D
  Placement = pos=(34,34,2.4) rot=(0,0,1;0rad)
  Radius = 3.35
FEATURE [Part::Sphere] Sphere030
  Angle1 = -90
  Angle2 = 90
  Angle3 = 360
  AttacherType = Attacher::AttachEngine3D
  Placement = pos=(0,0,4.3) rot=(1,0,0;3.14159rad)
  Radius = 3.35
FEATURE [Part::Sphere] Sphere031
  Angle1 = -90
  Angle2 = 90
  Angle3 = 360
  AttacherType = Attacher::AttachEngine3D
  Placement = pos=(20,34,4.3) rot=(1,0,0;3.14159rad)
  Radius = 3.35
FEATURE [Part::Sphere] Sphere032
  Angle1 = -90
  Angle2 = 90
  Angle3 = 360
  AttacherType = Attacher::AttachEngine3D
  Placement = pos=(6,34,2.4) rot=(0,0,1;0rad)
  Radius = 3.35
FEATURE [Part::Sphere] Sphere033
  Angle1 = -90
  Angle2 = 90
  Angle3 = 360
  AttacherType = Attacher::AttachEngine3D
  Placement = pos=(6,20,2.4) rot=(0,0,1;0rad)
  Radius = 3.35
FEATURE [Part::Sphere] Sphere034
  Angle1 = -90
  Angle2 = 90
  Angle3 = 360
  AttacherType = Attacher::AttachEngine3D
  Placement = pos=(20,34,2.4) rot=(0,0,1;0rad)
  Radius = 3.35
FEATURE [Part::Box] Box076  label="Cube060"
  AttacherType = Attacher::AttachEngine3D
  Height = 15
  Length = 19.5
  Placement = pos=(-9.75,-9.75,-3) rot=(0,0,1;0rad)
  Width = 19.5
FEATURE [Part::Box] Box077  label="Cube061"
  AttacherType = Attacher::AttachEngine3D
  Height = 15
  Length = 11
  Placement = pos=(8,24,-3) rot=(0,0,1;0.785398rad)
  Width = 11
FEATURE [Part::Box] Box078  label="Cube062"
  AttacherType = Attacher::AttachEngine3D
  Height = 15
  Length = 11
  Placement = pos=(8,0,-3) rot=(0,0,1;0.785398rad)
  Width = 11
FEATURE [Part::Box] Box079  label="Cube063"
  AttacherType = Attacher::AttachEngine3D
  Height = 15
  Length = 11
  Placement = pos=(32,0,-3) rot=(0,0,1;0.785398rad)
  Width = 11
FEATURE [Part::Box] Box080  label="Cube064"
  AttacherType = Attacher::AttachEngine3D
  Height = 15
  Length = 11
  Placement = pos=(32,24,-3) rot=(0,0,1;0.785398rad)
  Width = 11
FEATURE [Part::MultiFuse] Fusion022
  Shapes = -> [Box078,Box077,Box079,Box080]
FEATURE [Part::Cylinder] Cylinder020
  Angle = 360
  AttacherType = Attacher::AttachEngine3D
  Height = 20
  Placement = pos=(29.5,10.5,-5) rot=(0,0,1;0rad)
  Radius = 1.9
FEATURE [Part::Cylinder] Cylinder021
  Angle = 360
  AttacherType = Attacher::AttachEngine3D
  Height = 20
  Placement = pos=(10,29.5,-7) rot=(0,0,1;0rad)
  Radius = 1.9
FEATURE [Part::Cylinder] Cylinder022
  Angle = 360
  AttacherType = Attacher::AttachEngine3D
  Height = 20
  Placement = pos=(10,10.5,-5) rot=(0,0,1;0rad)
  Radius = 1.9
FEATURE [Part::Cylinder] Cylinder023
  Angle = 360
  AttacherType = Attacher::AttachEngine3D
  Height = 20
  Placement = pos=(29.5,29.5,-5) rot=(0,0,1;0rad)
  Radius = 1.9
FEATURE [Part::MultiFuse] Fusion023  label="M2 Screw holes001"
  Shapes = -> [Cylinder022,Cylinder020,Cylinder021,Cylinder023]
FEATURE [App::DocumentObjectGroup] Group  label="Cubes"
  Group = -> [Fusion017,Fusion022]
FEATURE [Part::Box] Box083  label="Cube067"
  AttacherType = Attacher::AttachEngine3D
  Height = 10
  Length = 24
  Placement = pos=(-12,-12,2.1) rot=(0,0,1;0rad)
  Width = 24
FEATURE [Part::Box] Box084  label="Cube068"
  AttacherType = Attacher::AttachEngine3D
  Height = 14
  Length = 20
  Placement = pos=(-10,-10,0) rot=(0,0,1;0rad)
  Width = 20
FEATURE [Part::Cut] Cut020
  Base = -> Box083
  Tool = -> Box084
FEATURE [Part::Chamfer] Chamfer007  label="Glue Channel Ball"
  Base = -> Cut020
  Edges = 8 edges r=0.95: [Edge4,Edge5,Edge14,Edge16,Edge17,Edge18,Edge19,Edge20]
FEATURE [Part::Chamfer] Chamfer008  label="Octogon Ball"
  Base = -> Box076
  Edges = 4 edges r=4: [Edge1,Edge3,Edge5,Edge7]
FEATURE [Part::Box] Box085  label="Cube069"
  AttacherType = Attacher::AttachEngine3D
  Height = 15
  Length = 19.5
  Placement = pos=(-9.75,-9.75,-14) rot=(0,0,1;0rad)
  Width = 19.5
FEATURE [Part::Box] Box086  label="Cube070"
  AttacherType = Attacher::AttachEngine3D
  Height = 10
  Length = 10
  Placement = pos=(4,-26,1) rot=(0.205904,-0.974848,-0.085288;0.803573rad)
  Width = 15
FEATURE [Part::Box] Box089  label="Cube073"
  AttacherType = Attacher::AttachEngine3D
  Height = 10
  Length = 10
  Placement = pos=(17,32.0919,9.95) rot=(-0.225436,0.969773,-0.093378;0.807337rad)
  Width = 15
FEATURE [Part::Box] Box090  label="Cube074"
  AttacherType = Attacher::AttachEngine3D
  Height = 10
  Length = 15
  Placement = pos=(30.8481,15.8,2.86019) rot=(0.974848,0.205904,-0.085288;0.803573rad)
  Width = 10
FEATURE [Part::Box] Box091  label="Cube075"
  AttacherType = Attacher::AttachEngine3D
  Height = 10
  Length = 10
  Placement = pos=(7.9081,17,9.95) rot=(-0.450607,0.280623,0.847469;1.65638rad)
  Width = 15
FEATURE [Part::Box] Box092  label="Cube076"
  AttacherType = Attacher::AttachEngine3D
  Height = 10
  Length = 10
  Placement = pos=(23,7.9081,9.95) rot=(-0.381178,-0.08861,0.920245;3.06822rad)
  Width = 15
FEATURE [Part::Box] Box093  label="Cube077"
  AttacherType = Attacher::AttachEngine3D
  Height = 7
  Length = 5
  Width = 40
FEATURE [Part::Box] Box094  label="Cube078"
  AttacherType = Attacher::AttachEngine3D
  Height = 7
  Length = 10
  Placement = pos=(-10,6,0) rot=(0,0,1;0rad)
  Width = 2
FEATURE [Part::Box] Box095  label="Cube079"
  AttacherType = Attacher::AttachEngine3D
  Height = 7
  Length = 10
  Placement = pos=(-10,10,0) rot=(0,0,1;0rad)
  Width = 2
FEATURE [Part::Box] Box096  label="Cube080"
  AttacherType = Attacher::AttachEngine3D
  Height = 7
  Length = 10
  Placement = pos=(-10,25.4,0) rot=(0,0,1;0rad)
  Width = 2
FEATURE [Part::Box] Box097  label="Cube081"
  AttacherType = Attacher::AttachEngine3D
  Height = 7
  Length = 10
  Placement = pos=(-10,34.6,0) rot=(0,0,1;0rad)
  Width = 2
FEATURE [Part::Sphere] Sphere035
  Angle1 = -90
  Angle2 = 90
  Angle3 = 360
  AttacherType = Attacher::AttachEngine3D
  Placement = pos=(-3,6.5,2.5) rot=(0,0,1;0rad)
  Radius = 1.25
FEATURE [Part::Box] Box098  label="Cube082"
  AttacherType = Attacher::AttachEngine3D
  Height = 10
  Length = 13
  Placement = pos=(-10.19,0,-1.19) rot=(0,-1,0;0.785398rad)
  Width = 40
FEATURE [Part::Sphere] Sphere036
  Angle1 = -90
  Angle2 = 90
  Angle3 = 360
  AttacherType = Attacher::AttachEngine3D
  Placement = pos=(-3,11.5,2.5) rot=(0,0,1;0rad)
  Radius = 1.25
FEATURE [Part::Sphere] Sphere037
  Angle1 = -90
  Angle2 = 90
  Angle3 = 360
  AttacherType = Attacher::AttachEngine3D
  Placement = pos=(-3,28,2.5) rot=(0,0,1;0rad)
  Radius = 1.5
FEATURE [Part::Sphere] Sphere038
  Angle1 = -90
  Angle2 = 90
  Angle3 = 360
  AttacherType = Attacher::AttachEngine3D
  Placement = pos=(-3,34,2.5) rot=(0,0,1;0rad)
  Radius = 1.5
FEATURE [Part::MultiFuse] Fusion030
  Shapes = -> [Box093,Box094,Box095,Box096,Box097]
FEATURE [Part::Cut] Cut025
  Base = -> Fusion030
  Tool = -> Box098
FEATURE [Part::MultiFuse] Fusion031
  Shapes = -> [Sphere035,Sphere036,Cut025]
FEATURE [Part::MultiFuse] Fusion032
  Shapes = -> [Sphere038,Sphere037]
FEATURE [Part::Cut] Cut026
  Base = -> Fusion031
  Tool = -> Fusion032
FEATURE [Part::Chamfer] Chamfer009
  Base = -> Cut026
  Edges = 4 edges r=4: [Edge31,Edge37,Edge43,Edge46]
FEATURE [Part::Box] Box099  label="Cube083"
  AttacherType = Attacher::AttachEngine3D
  Height = 7
  Length = 4
  Placement = pos=(-1,5,0) rot=(0,0,1;0rad)
  Width = 1
FEATURE [Part::Box] Box100  label="Cube084"
  AttacherType = Attacher::AttachEngine3D
  Height = 7
  Length = 4
  Placement = pos=(-1,8,0) rot=(0,0,1;0rad)
  Width = 2
FEATURE [Part::Box] Box101  label="Cube085"
  AttacherType = Attacher::AttachEngine3D
  Height = 7
  Length = 4
  Placement = pos=(-1,12,0) rot=(0,0,1;0rad)
  Width = 1
FEATURE [Part::Box] Box102  label="Cube086"
  AttacherType = Attacher::AttachEngine3D
  Height = 7
  Length = 4
  Placement = pos=(-1,24.4,0) rot=(0,0,1;0rad)
  Width = 1
FEATURE [Part::Box] Box103  label="Cube087"
  AttacherType = Attacher::AttachEngine3D
  Height = 7
  Length = 4
  Placement = pos=(-1,36.6,0) rot=(0,0,1;0rad)
  Width = 1
FEATURE [Part::Box] Box104  label="Cube088"
  AttacherType = Attacher::AttachEngine3D
  Height = 7
  Length = 4
  Placement = pos=(-1,27.4,0) rot=(0,0,1;0rad)
  Width = 7.2
FEATURE [Part::MultiFuse] Fusion033
  Shapes = -> [Box104,Box101,Box103,Box100,Box102,Box099]
FEATURE [Part::Cut] Cut027
  Base = -> Chamfer009
  Placement = pos=(-5,40,3) rot=(1,0,0;3.14159rad)
  Tool = -> Fusion033
FEATURE [Part::Box] Box105  label="Cube089"
  AttacherType = Attacher::AttachEngine3D
  Height = 10
  Length = 12
  Placement = pos=(-11,-2,-12) rot=(0,0,1;0rad)
  Width = 44
FEATURE [Part::Cut] Cut028
  Base = -> Cut027
  Tool = -> Box105
FEATURE [Part::Box] Box106  label="Cube090"
  AttacherType = Attacher::AttachEngine3D
  Height = 7
  Length = 10
  Placement = pos=(-10,34.6,0) rot=(0,0,1;0rad)
  Width = 2
FEATURE [Part::Box] Box107  label="Cube091"
  AttacherType = Attacher::AttachEngine3D
  Height = 7
  Length = 5
  Width = 40
FEATURE [Part::Box] Box108  label="Cube092"
  AttacherType = Attacher::AttachEngine3D
  Height = 7
  Length = 10
  Placement = pos=(-10,25.4,0) rot=(0,0,1;0rad)
  Width = 2
FEATURE [Part::Box] Box109  label="Cube093"
  AttacherType = Attacher::AttachEngine3D
  Height = 7
  Length = 10
  Placement = pos=(-10,10,0) rot=(0,0,1;0rad)
  Width = 2
FEATURE [Part::Box] Box110  label="Cube094"
  AttacherType = Attacher::AttachEngine3D
  Height = 7
  Length = 10
  Placement = pos=(-10,6,0) rot=(0,0,1;0rad)
  Width = 2
FEATURE [Part::Sphere] Sphere039
  Angle1 = -90
  Angle2 = 90
  Angle3 = 360
  AttacherType = Attacher::AttachEngine3D
  Placement = pos=(-3,6.5,2.5) rot=(0,0,1;0rad)
  Radius = 1.25
FEATURE [Part::Box] Box111  label="Cube095"
  AttacherType = Attacher::AttachEngine3D
  Height = 10
  Length = 13
  Placement = pos=(-10.19,0,-1.19) rot=(0,-1,0;0.785398rad)
  Width = 40
FEATURE [Part::Sphere] Sphere040
  Angle1 = -90
  Angle2 = 90
  Angle3 = 360
  AttacherType = Attacher::AttachEngine3D
  Placement = pos=(-3,11.5,2.5) rot=(0,0,1;0rad)
  Radius = 1.25
FEATURE [Part::Sphere] Sphere041
  Angle1 = -90
  Angle2 = 90
  Angle3 = 360
  AttacherType = Attacher::AttachEngine3D
  Placement = pos=(-3,28,2.5) rot=(0,0,1;0rad)
  Radius = 1.5
FEATURE [Part::Sphere] Sphere042
  Angle1 = -90
  Angle2 = 90
  Angle3 = 360
  AttacherType = Attacher::AttachEngine3D
  Placement = pos=(-3,34,2.5) rot=(0,0,1;0rad)
  Radius = 1.5
FEATURE [Part::MultiFuse] Fusion034
  Shapes = -> [Box107,Box110,Box109,Box108,Box106]
FEATURE [Part::Cut] Cut029
  Base = -> Fusion034
  Tool = -> Box111
FEATURE [Part::MultiFuse] Fusion035
  Shapes = -> [Sphere039,Sphere040,Cut029]
FEATURE [Part::MultiFuse] Fusion036
  Shapes = -> [Sphere042,Sphere041]
FEATURE [Part::Cut] Cut030
  Base = -> Fusion035
  Tool = -> Fusion036
FEATURE [Part::Chamfer] Chamfer010
  Base = -> Cut030
  Edges = 4 edges r=4: [Edge31,Edge37,Edge43,Edge46]
FEATURE [Part::Box] Box112  label="Cube096"
  AttacherType = Attacher::AttachEngine3D
  Height = 7
  Length = 4
  Placement = pos=(-1,5,0) rot=(0,0,1;0rad)
  Width = 1
FEATURE [Part::Box] Box113  label="Cube097"
  AttacherType = Attacher::AttachEngine3D
  Height = 7
  Length = 4
  Placement = pos=(-1,8,0) rot=(0,0,1;0rad)
  Width = 2
FEATURE [Part::Box] Box114  label="Cube098"
  AttacherType = Attacher::AttachEngine3D
  Height = 7
  Length = 4
  Placement = pos=(-1,12,0) rot=(0,0,1;0rad)
  Width = 1
FEATURE [Part::Box] Box115  label="Cube099"
  AttacherType = Attacher::AttachEngine3D
  Height = 7
  Length = 4
  Placement = pos=(-1,24.4,0) rot=(0,0,1;0rad)
  Width = 1
FEATURE [Part::Box] Box116  label="Cube100"
  AttacherType = Attacher::AttachEngine3D
  Height = 7
  Length = 4
  Placement = pos=(-1,36.6,0) rot=(0,0,1;0rad)
  Width = 1
FEATURE [Part::Box] Box117  label="Cube101"
  AttacherType = Attacher::AttachEngine3D
  Height = 7
  Length = 4
  Placement = pos=(-1,27.4,0) rot=(0,0,1;0rad)
  Width = 7.2
FEATURE [Part::MultiFuse] Fusion037
  Shapes = -> [Box117,Box114,Box116,Box113,Box115,Box112]
FEATURE [Part::Cut] Cut031
  Base = -> Chamfer010
  Placement = pos=(-5,40,3) rot=(1,0,0;3.14159rad)
  Tool = -> Fusion037
FEATURE [Part::Box] Box118  label="Cube102"
  AttacherType = Attacher::AttachEngine3D
  Height = 10
  Length = 12
  Placement = pos=(-11,-2,-12) rot=(0,0,1;0rad)
  Width = 44
FEATURE [Part::Cut] Cut032
  Base = -> Cut031
  Placement = pos=(40,0,0) rot=(0,0,1;1.5708rad)
  Tool = -> Box118
FEATURE [Part::Box] Box119  label="Cube103"
  AttacherType = Attacher::AttachEngine3D
  Height = 7
  Length = 4
  Placement = pos=(-1,12,0) rot=(0,0,1;0rad)
  Width = 1
FEATURE [Part::Box] Box120  label="Cube104"
  AttacherType = Attacher::AttachEngine3D
  Height = 10
  Length = 13
  Placement = pos=(-10.19,0,-1.19) rot=(0,-1,0;0.785398rad)
  Width = 40
FEATURE [Part::Box] Box121  label="Cube105"
  AttacherType = Attacher::AttachEngine3D
  Height = 7
  Length = 4
  Placement = pos=(-1,27.4,0) rot=(0,0,1;0rad)
  Width = 7.2
FEATURE [Part::Box] Box122  label="Cube106"
  AttacherType = Attacher::AttachEngine3D
  Height = 7
  Length = 4
  Placement = pos=(-1,5,0) rot=(0,0,1;0rad)
  Width = 1
FEATURE [Part::Box] Box123  label="Cube107"
  AttacherType = Attacher::AttachEngine3D
  Height = 7
  Length = 10
  Placement = pos=(-10,6,0) rot=(0,0,1;0rad)
  Width = 2
FEATURE [Part::Box] Box124  label="Cube108"
  AttacherType = Attacher::AttachEngine3D
  Height = 10
  Length = 12
  Placement = pos=(-11,-2,-12) rot=(0,0,1;0rad)
  Width = 44
FEATURE [Part::Sphere] Sphere043
  Angle1 = -90
  Angle2 = 90
  Angle3 = 360
  AttacherType = Attacher::AttachEngine3D
  Placement = pos=(-3,6.5,2.5) rot=(0,0,1;0rad)
  Radius = 1.25
FEATURE [Part::Box] Box125  label="Cube109"
  AttacherType = Attacher::AttachEngine3D
  Height = 7
  Length = 10
  Placement = pos=(-10,25.4,0) rot=(0,0,1;0rad)
  Width = 2
FEATURE [Part::Box] Box126  label="Cube110"
  AttacherType = Attacher::AttachEngine3D
  Height = 7
  Length = 10
  Placement = pos=(-10,10,0) rot=(0,0,1;0rad)
  Width = 2
FEATURE [Part::Sphere] Sphere044
  Angle1 = -90
  Angle2 = 90
  Angle3 = 360
  AttacherType = Attacher::AttachEngine3D
  Placement = pos=(-3,28,2.5) rot=(0,0,1;0rad)
  Radius = 1.5
FEATURE [Part::Sphere] Sphere045
  Angle1 = -90
  Angle2 = 90
  Angle3 = 360
  AttacherType = Attacher::AttachEngine3D
  Placement = pos=(-3,11.5,2.5) rot=(0,0,1;0rad)
  Radius = 1.25
FEATURE [Part::Box] Box127  label="Cube111"
  AttacherType = Attacher::AttachEngine3D
  Height = 7
  Length = 4
  Placement = pos=(-1,36.6,0) rot=(0,0,1;0rad)
  Width = 1
FEATURE [Part::Sphere] Sphere046
  Angle1 = -90
  Angle2 = 90
  Angle3 = 360
  AttacherType = Attacher::AttachEngine3D
  Placement = pos=(-3,34,2.5) rot=(0,0,1;0rad)
  Radius = 1.5
FEATURE [Part::MultiFuse] Fusion040
  Shapes = -> [Sphere046,Sphere044]
FEATURE [Part::Box] Box128  label="Cube112"
  AttacherType = Attacher::AttachEngine3D
  Height = 7
  Length = 4
  Placement = pos=(-1,8,0) rot=(0,0,1;0rad)
  Width = 2
FEATURE [Part::Box] Box129  label="Cube113"
  AttacherType = Attacher::AttachEngine3D
  Height = 7
  Length = 10
  Placement = pos=(-10,34.6,0) rot=(0,0,1;0rad)
  Width = 2
FEATURE [Part::Box] Box130  label="Cube114"
  AttacherType = Attacher::AttachEngine3D
  Height = 7
  Length = 4
  Placement = pos=(-1,24.4,0) rot=(0,0,1;0rad)
  Width = 1
FEATURE [Part::MultiFuse] Fusion038
  Shapes = -> [Box121,Box119,Box127,Box128,Box130,Box122]
FEATURE [Part::Box] Box131  label="Cube115"
  AttacherType = Attacher::AttachEngine3D
  Height = 7
  Length = 5
  Width = 40
FEATURE [Part::MultiFuse] Fusion041
  Shapes = -> [Box131,Box123,Box126,Box125,Box129]
FEATURE [Part::Cut] Cut035
  Base = -> Fusion041
  Tool = -> Box120
FEATURE [Part::MultiFuse] Fusion039
  Shapes = -> [Sphere043,Sphere045,Cut035]
FEATURE [Part::Cut] Cut036
  Base = -> Fusion039
  Tool = -> Fusion040
FEATURE [Part::Chamfer] Chamfer011
  Base = -> Cut036
  Edges = 4 edges r=4: [Edge31,Edge37,Edge43,Edge46]
FEATURE [Part::Cut] Cut034
  Base = -> Chamfer011
  Placement = pos=(-5,40,3) rot=(1,0,0;3.14159rad)
  Tool = -> Fusion038
FEATURE [Part::Cut] Cut033
  Base = -> Cut034
  Placement = pos=(40,40,0) rot=(0,0,1;3.14159rad)
  Tool = -> Box124
FEATURE [Part::Sphere] Sphere047
  Angle1 = -90
  Angle2 = 90
  Angle3 = 360
  AttacherType = Attacher::AttachEngine3D
  Placement = pos=(-3,11.5,2.5) rot=(0,0,1;0rad)
  Radius = 1.25
FEATURE [Part::Box] Box132  label="Cube116"
  AttacherType = Attacher::AttachEngine3D
  Height = 7
  Length = 10
  Placement = pos=(-10,6,0) rot=(0,0,1;0rad)
  Width = 2
FEATURE [Part::Box] Box133  label="Cube117"
  AttacherType = Attacher::AttachEngine3D
  Height = 7
  Length = 4
  Placement = pos=(-1,8,0) rot=(0,0,1;0rad)
  Width = 2
FEATURE [Part::Box] Box134  label="Cube118"
  AttacherType = Attacher::AttachEngine3D
  Height = 7
  Length = 10
  Placement = pos=(-10,10,0) rot=(0,0,1;0rad)
  Width = 2
FEATURE [Part::Box] Box135  label="Cube119"
  AttacherType = Attacher::AttachEngine3D
  Height = 10
  Length = 12
  Placement = pos=(-11,-2,-12) rot=(0,0,1;0rad)
  Width = 44
FEATURE [Part::Box] Box136  label="Cube120"
  AttacherType = Attacher::AttachEngine3D
  Height = 7
  Length = 4
  Placement = pos=(-1,5,0) rot=(0,0,1;0rad)
  Width = 1
FEATURE [Part::Sphere] Sphere048
  Angle1 = -90
  Angle2 = 90
  Angle3 = 360
  AttacherType = Attacher::AttachEngine3D
  Placement = pos=(-3,28,2.5) rot=(0,0,1;0rad)
  Radius = 1.5
FEATURE [Part::Sphere] Sphere049
  Angle1 = -90
  Angle2 = 90
  Angle3 = 360
  AttacherType = Attacher::AttachEngine3D
  Placement = pos=(-3,6.5,2.5) rot=(0,0,1;0rad)
  Radius = 1.25
FEATURE [Part::Sphere] Sphere050
  Angle1 = -90
  Angle2 = 90
  Angle3 = 360
  AttacherType = Attacher::AttachEngine3D
  Placement = pos=(-3,34,2.5) rot=(0,0,1;0rad)
  Radius = 1.5
FEATURE [Part::Box] Box137  label="Cube121"
  AttacherType = Attacher::AttachEngine3D
  Height = 7
  Length = 4
  Placement = pos=(-1,12,0) rot=(0,0,1;0rad)
  Width = 1
FEATURE [Part::Box] Box138  label="Cube122"
  AttacherType = Attacher::AttachEngine3D
  Height = 7
  Length = 5
  Width = 40
FEATURE [Part::Box] Box139  label="Cube123"
  AttacherType = Attacher::AttachEngine3D
  Height = 7
  Length = 4
  Placement = pos=(-1,36.6,0) rot=(0,0,1;0rad)
  Width = 1
FEATURE [Part::Box] Box140  label="Cube124"
  AttacherType = Attacher::AttachEngine3D
  Height = 7
  Length = 4
  Placement = pos=(-1,24.4,0) rot=(0,0,1;0rad)
  Width = 1
FEATURE [Part::Box] Box141  label="Cube125"
  AttacherType = Attacher::AttachEngine3D
  Height = 7
  Length = 10
  Placement = pos=(-10,25.4,0) rot=(0,0,1;0rad)
  Width = 2
FEATURE [Part::Box] Box142  label="Cube126"
  AttacherType = Attacher::AttachEngine3D
  Height = 10
  Length = 13
  Placement = pos=(-10.19,0,-1.19) rot=(0,-1,0;0.785398rad)
  Width = 40
FEATURE [Part::Box] Box143  label="Cube127"
  AttacherType = Attacher::AttachEngine3D
  Height = 7
  Length = 10
  Placement = pos=(-10,34.6,0) rot=(0,0,1;0rad)
  Width = 2
FEATURE [Part::MultiFuse] Fusion044
  Shapes = -> [Box138,Box132,Box134,Box141,Box143]
FEATURE [Part::Cut] Cut037
  Base = -> Fusion044
  Tool = -> Box142
FEATURE [Part::MultiFuse] Fusion042
  Shapes = -> [Sphere049,Sphere047,Cut037]
FEATURE [Part::MultiFuse] Fusion045
  Shapes = -> [Sphere050,Sphere048]
FEATURE [Part::Cut] Cut038
  Base = -> Fusion042
  Tool = -> Fusion045
FEATURE [Part::Chamfer] Chamfer012
  Base = -> Cut038
  Edges = 4 edges r=4: [Edge31,Edge37,Edge43,Edge46]
FEATURE [Part::Box] Box144  label="Cube128"
  AttacherType = Attacher::AttachEngine3D
  Height = 7
  Length = 4
  Placement = pos=(-1,27.4,0) rot=(0,0,1;0rad)
  Width = 7.2
FEATURE [Part::MultiFuse] Fusion043
  Shapes = -> [Box144,Box137,Box139,Box133,Box140,Box136]
FEATURE [Part::Cut] Cut040
  Base = -> Chamfer012
  Placement = pos=(-5,40,3) rot=(1,0,0;3.14159rad)
  Tool = -> Fusion043
FEATURE [Part::Cut] Cut039
  Base = -> Cut040
  Placement = pos=(0,40,0) rot=(0,0,-1;1.5708rad)
  Tool = -> Box135
FEATURE [Part::MultiFuse] Fusion048
  Shapes = -> [Box089,Box091,Box090,Box092]
FEATURE [Part::Box] Box145  label="Cube129"
  AttacherType = Attacher::AttachEngine3D
  Height = 15
  Length = 19.5
  Placement = pos=(-9.75,-9.75,-14) rot=(0,0,1;0rad)
  Width = 19.5
FEATURE [Part::Box] Box146  label="Cube130"
  AttacherType = Attacher::AttachEngine3D
  Height = 15
  Length = 19.5
  Placement = pos=(-9.75,-9.75,-3) rot=(0,0,1;0rad)
  Width = 19.5
FEATURE [Part::Chamfer] Chamfer013  label="Octagon"
  Base = -> Box146
  Edges = 4 edges r=4: [Edge1,Edge3,Edge5,Edge7]
FEATURE [Part::Box] Box147  label="Cube131"
  AttacherType = Attacher::AttachEngine3D
  Height = 10
  Length = 24
  Placement = pos=(-12,-12,2.1) rot=(0,0,1;0rad)
  Width = 24
FEATURE [Part::Box] Box148  label="Cube132"
  AttacherType = Attacher::AttachEngine3D
  Height = 14
  Length = 20
  Placement = pos=(-10,-10,0) rot=(0,0,1;0rad)
  Width = 20
FEATURE [Part::Cut] Cut043
  Base = -> Box147
  Tool = -> Box148
FEATURE [Part::Chamfer] Chamfer014  label="Glue Channel"
  Base = -> Cut043
  Edges = 8 edges r=0.95: [Edge4,Edge5,Edge14,Edge16,Edge17,Edge18,Edge19,Edge20]
FEATURE [Part::Cut] Cut047
  Base = -> Cut003
  Tool = -> Chamfer007
FEATURE [Part::Cylinder] Cylinder024
  Angle = 360
  AttacherType = Attacher::AttachEngine3D
  Height = 10
  Placement = pos=(-15,-15,-5) rot=(0,0,1;0rad)
  Radius = 1.7
FEATURE [Part::Cylinder] Cylinder025
  Angle = 360
  AttacherType = Attacher::AttachEngine3D
  Height = 10
  Placement = pos=(15,0,-5) rot=(0,0,1;0rad)
  Radius = 1.7
FEATURE [Part::Cylinder] Cylinder026
  Angle = 360
  AttacherType = Attacher::AttachEngine3D
  Height = 10
  Placement = pos=(-15,15,-5) rot=(0,0,1;0rad)
  Radius = 1.7
FEATURE [Part::MultiFuse] Fusion052  label="Screw Holes to remove ball mags"
  Shapes = -> [Cylinder024,Cylinder025,Cylinder026]
FEATURE [Drawing::FeatureViewAnnotation] Annotation
  Font = Sans
  Rotation = 0
  Scale = 7
  Text = 0.4Added in Holes to Mag plate for removal of magnet
  ViewResult = <g transform="translate(14,23) rotate(0)">\n<text id="Annotation"\n font-family="Sans"\n font-size="7"\n fill="#000000">\n<tspan x="0" dy="1em">0.4Added in Holes to Mag plate for removal of magnet</tspan>\n</text>\n</g>
  Visible = false
  X = 14
  Y = 23
FEATURE [Part::Box] Box149  label="Re-level Edge Clip Block001"
  AttacherType = Attacher::AttachEngine3D
  Height = 10
  Length = 12
  Placement = pos=(-21.5,-2,-7) rot=(0,0,1;0rad)
  Width = 44
FEATURE [Part::Fuse] Fusion  label="Bumps"
  Base = -> Sphere008
  Tool = -> Sphere009
FEATURE [Part::Fuse] Fusion053  label="Holes"
  Base = -> Sphere010
  Tool = -> Sphere011
FEATURE [Part::MultiFuse] Fusion054
  Shapes = -> [Box001,Box002,Box003,Box004,Box005]
FEATURE [Part::Fuse] Fusion055
  Base = -> Fusion
  Tool = -> Fusion054
FEATURE [Part::Cut] Cut
  Base = -> Fusion055
  Tool = -> Fusion053
FEATURE [Part::Cut] Cut056
  Base = -> Cut
  Tool = -> Fusion003
FEATURE [Part::Cut] Cut057
  Base = -> Cut056
  Tool = -> Box013
FEATURE [Part::Cut] Cut058
  Base = -> Cut057
  Tool = -> Box149
FEATURE [Part::Cut] Cut059  label="Edge Clips Master"
  Base = -> Cut058
  Placement = pos=(-20,-20,0) rot=(0,0,1;0rad)
  Tool = -> Box006
FEATURE [Part::Box] Box150  label="Cube133"
  AttacherType = Attacher::AttachEngine3D
  Height = 7
  Length = 5
  Placement = pos=(-5,0,-2) rot=(0,0,1;0rad)
  Width = 40
FEATURE [Part::Box] Box151  label="Cube134"
  AttacherType = Attacher::AttachEngine3D
  Height = 7
  Length = 10
  Placement = pos=(-15,6,-2) rot=(0,0,1;0rad)
  Width = 2
FEATURE [Part::Box] Box152  label="Cube135"
  AttacherType = Attacher::AttachEngine3D
  Height = 7
  Length = 10
  Placement = pos=(-15,10,-2) rot=(0,0,1;0rad)
  Width = 2
FEATURE [Part::Box] Box153  label="Cube136"
  AttacherType = Attacher::AttachEngine3D
  Height = 7
  Length = 10
  Placement = pos=(-15,25.4,-2) rot=(0,0,1;0rad)
  Width = 2
FEATURE [Part::Box] Box154  label="Cube137"
  AttacherType = Attacher::AttachEngine3D
  Height = 7
  Length = 10
  Placement = pos=(-15,34.6,-2) rot=(0,0,1;0rad)
  Width = 2
FEATURE [Part::Sphere] Sphere051
  Angle1 = -90
  Angle2 = 90
  Angle3 = 360
  AttacherType = Attacher::AttachEngine3D
  Placement = pos=(-7.5,6.5,0.5) rot=(0,0,1;0rad)
  Radius = 1.25
FEATURE [Part::Box] Box155  label="Chamfer Cube001"
  AttacherType = Attacher::AttachEngine3D
  Height = 10
  Length = 13
  Placement = pos=(-11.69,0,-1.19) rot=(0,-1,0;0.785398rad)
  Width = 40
FEATURE [Part::Sphere] Sphere052
  Angle1 = -90
  Angle2 = 90
  Angle3 = 360
  AttacherType = Attacher::AttachEngine3D
  Placement = pos=(-7.5,11.5,0.5) rot=(0,0,1;0rad)
  Radius = 1.25
FEATURE [Part::Sphere] Sphere053
  Angle1 = -90
  Angle2 = 90
  Angle3 = 360
  AttacherType = Attacher::AttachEngine3D
  Placement = pos=(-7.5,28,0.5) rot=(0,0,1;0rad)
  Radius = 1.5
FEATURE [Part::Sphere] Sphere054
  Angle1 = -90
  Angle2 = 90
  Angle3 = 360
  AttacherType = Attacher::AttachEngine3D
  Placement = pos=(-7.5,34,0.5) rot=(0,0,1;0rad)
  Radius = 1.5
FEATURE [Part::Box] Box156  label="Cube138"
  AttacherType = Attacher::AttachEngine3D
  Height = 7
  Length = 4
  Placement = pos=(-6,5,-2) rot=(0,0,1;0rad)
  Width = 1
FEATURE [Part::Box] Box157  label="Cube139"
  AttacherType = Attacher::AttachEngine3D
  Height = 7
  Length = 4
  Placement = pos=(-6,8,-2) rot=(0,0,1;0rad)
  Width = 2
FEATURE [Part::Box] Box158  label="Cube140"
  AttacherType = Attacher::AttachEngine3D
  Height = 7
  Length = 4
  Placement = pos=(-6,12,-2) rot=(0,0,1;0rad)
  Width = 1
FEATURE [Part::Box] Box159  label="Cube141"
  AttacherType = Attacher::AttachEngine3D
  Height = 7
  Length = 4
  Placement = pos=(-6,24.4,-2) rot=(0,0,1;0rad)
  Width = 1
FEATURE [Part::Box] Box160  label="Cube142"
  AttacherType = Attacher::AttachEngine3D
  Height = 7
  Length = 4
  Placement = pos=(-6,36.6,-2) rot=(0,0,1;0rad)
  Width = 1
FEATURE [Part::Box] Box161  label="Cube143"
  AttacherType = Attacher::AttachEngine3D
  Height = 7
  Length = 4
  Placement = pos=(-6,27.4,-2) rot=(0,0,1;0rad)
  Width = 7.2
FEATURE [Part::MultiFuse] Fusion056  label="Extra Holes for Clips001"
  Shapes = -> [Box161,Box158,Box160,Box157,Box159,Box156]
FEATURE [Part::Box] Box162  label="Re-level Edge Clip Block002"
  AttacherType = Attacher::AttachEngine3D
  Height = 10
  Length = 20
  Placement = pos=(-19,-2,3) rot=(0,0,1;0rad)
  Width = 44
FEATURE [Part::Box] Box163  label="Re-level Edge Clip Block003"
  AttacherType = Attacher::AttachEngine3D
  Height = 10
  Length = 12
  Placement = pos=(-21.5,-2,-7) rot=(0,0,1;0rad)
  Width = 44
FEATURE [Part::Fuse] Fusion057  label="Bumps001"
  Base = -> Sphere051
  Tool = -> Sphere052
FEATURE [Part::Fuse] Fusion058  label="Holes001"
  Base = -> Sphere053
  Tool = -> Sphere054
FEATURE [Part::MultiFuse] Fusion059
  Shapes = -> [Box150,Box151,Box152,Box153,Box154]
FEATURE [Part::Fuse] Fusion060
  Base = -> Fusion057
  Tool = -> Fusion059
FEATURE [Part::Cut] Cut060
  Base = -> Fusion060
  Tool = -> Fusion058
FEATURE [Part::Cut] Cut061
  Base = -> Cut060
  Tool = -> Fusion056
FEATURE [Part::Cut] Cut062
  Base = -> Cut061
  Tool = -> Box162
FEATURE [Part::Cut] Cut063
  Base = -> Cut062
  Tool = -> Box163
FEATURE [Part::Cut] Cut064  label="Copy Edge Clip"
  Base = -> Cut063
  Placement = pos=(-27,20,-7) rot=(0.707107,0,-0.707107;3.14159rad)
  Tool = -> Box155
FEATURE [App::DocumentObjectGroup] Group001  label="Old"
  Group = -> [Cut008,Cut009,Cut015,Cut018,Fusion021,Fusion023,Group,Cut039,Cut028,Cut032,Cut033,Fusion048]
FEATURE [Part::Box] Box164  label="Cube144"
  AttacherType = Attacher::AttachEngine3D
  Height = 7
  Length = 5
  Placement = pos=(-5,0,-2) rot=(0,0,1;0rad)
  Width = 40
FEATURE [Part::Box] Box165  label="Cube145"
  AttacherType = Attacher::AttachEngine3D
  Height = 7
  Length = 10
  Placement = pos=(-15,6,-2) rot=(0,0,1;0rad)
  Width = 2
FEATURE [Part::Box] Box166  label="Cube146"
  AttacherType = Attacher::AttachEngine3D
  Height = 7
  Length = 10
  Placement = pos=(-15,10,-2) rot=(0,0,1;0rad)
  Width = 2
FEATURE [Part::Box] Box167  label="Cube147"
  AttacherType = Attacher::AttachEngine3D
  Height = 7
  Length = 10
  Placement = pos=(-15,25.4,-2) rot=(0,0,1;0rad)
  Width = 2
FEATURE [Part::Box] Box168  label="Cube148"
  AttacherType = Attacher::AttachEngine3D
  Height = 7
  Length = 10
  Placement = pos=(-15,34.6,-2) rot=(0,0,1;0rad)
  Width = 2
FEATURE [Part::Sphere] Sphere055
  Angle1 = -90
  Angle2 = 90
  Angle3 = 360
  AttacherType = Attacher::AttachEngine3D
  Placement = pos=(-7.5,6.5,0.5) rot=(0,0,1;0rad)
  Radius = 1.25
FEATURE [Part::Box] Box169  label="Chamfer Cube002"
  AttacherType = Attacher::AttachEngine3D
  Height = 10
  Length = 13
  Placement = pos=(-11.69,0,-1.19) rot=(0,-1,0;0.785398rad)
  Width = 40
FEATURE [Part::Sphere] Sphere056
  Angle1 = -90
  Angle2 = 90
  Angle3 = 360
  AttacherType = Attacher::AttachEngine3D
  Placement = pos=(-7.5,11.5,0.5) rot=(0,0,1;0rad)
  Radius = 1.25
FEATURE [Part::Sphere] Sphere057
  Angle1 = -90
  Angle2 = 90
  Angle3 = 360
  AttacherType = Attacher::AttachEngine3D
  Placement = pos=(-7.5,28,0.5) rot=(0,0,1;0rad)
  Radius = 1.5
FEATURE [Part::Sphere] Sphere058
  Angle1 = -90
  Angle2 = 90
  Angle3 = 360
  AttacherType = Attacher::AttachEngine3D
  Placement = pos=(-7.5,34,0.5) rot=(0,0,1;0rad)
  Radius = 1.5
FEATURE [Part::Box] Box170  label="Cube149"
  AttacherType = Attacher::AttachEngine3D
  Height = 7
  Length = 4
  Placement = pos=(-6,5,-2) rot=(0,0,1;0rad)
  Width = 1
FEATURE [Part::Box] Box171  label="Cube150"
  AttacherType = Attacher::AttachEngine3D
  Height = 7
  Length = 4
  Placement = pos=(-6,8,-2) rot=(0,0,1;0rad)
  Width = 2
FEATURE [Part::Box] Box172  label="Cube151"
  AttacherType = Attacher::AttachEngine3D
  Height = 7
  Length = 4
  Placement = pos=(-6,12,-2) rot=(0,0,1;0rad)
  Width = 1
FEATURE [Part::Box] Box173  label="Cube152"
  AttacherType = Attacher::AttachEngine3D
  Height = 7
  Length = 4
  Placement = pos=(-6,24.4,-2) rot=(0,0,1;0rad)
  Width = 1
FEATURE [Part::Box] Box174  label="Cube153"
  AttacherType = Attacher::AttachEngine3D
  Height = 7
  Length = 4
  Placement = pos=(-6,36.6,-2) rot=(0,0,1;0rad)
  Width = 1
FEATURE [Part::Box] Box175  label="Cube154"
  AttacherType = Attacher::AttachEngine3D
  Height = 7
  Length = 4
  Placement = pos=(-6,27.4,-2) rot=(0,0,1;0rad)
  Width = 7.2
FEATURE [Part::MultiFuse] Fusion061  label="Extra Holes for Clips002"
  Shapes = -> [Box175,Box172,Box174,Box171,Box173,Box170]
FEATURE [Part::Box] Box176  label="Re-level Edge Clip Block004"
  AttacherType = Attacher::AttachEngine3D
  Height = 10
  Length = 20
  Placement = pos=(-19,-2,3) rot=(0,0,1;0rad)
  Width = 44
FEATURE [Part::Box] Box177  label="Re-level Edge Clip Block005"
  AttacherType = Attacher::AttachEngine3D
  Height = 10
  Length = 12
  Placement = pos=(-21.5,-2,-7) rot=(0,0,1;0rad)
  Width = 44
FEATURE [Part::Fuse] Fusion062  label="Bumps002"
  Base = -> Sphere055
  Tool = -> Sphere056
FEATURE [Part::Fuse] Fusion063  label="Holes002"
  Base = -> Sphere057
  Tool = -> Sphere058
FEATURE [Part::MultiFuse] Fusion064
  Shapes = -> [Box164,Box165,Box166,Box167,Box168]
FEATURE [Part::Fuse] Fusion065
  Base = -> Fusion062
  Tool = -> Fusion064
FEATURE [Part::Cut] Cut065
  Base = -> Fusion065
  Tool = -> Fusion063
FEATURE [Part::Cut] Cut066
  Base = -> Cut065
  Tool = -> Fusion061
FEATURE [Part::Cut] Cut067
  Base = -> Cut066
  Tool = -> Box176
FEATURE [Part::Cut] Cut068
  Base = -> Cut067
  Tool = -> Box177
FEATURE [Part::Cut] Cut069  label="Edge Clips001"
  Base = -> Cut068
  Placement = pos=(20,-20,0) rot=(0,0,1;1.5708rad)
  Tool = -> Box169
FEATURE [Part::Box] Box178  label="Cube155"
  AttacherType = Attacher::AttachEngine3D
  Height = 7
  Length = 5
  Placement = pos=(-5,0,-2) rot=(0,0,1;0rad)
  Width = 40
FEATURE [Part::Box] Box179  label="Cube156"
  AttacherType = Attacher::AttachEngine3D
  Height = 7
  Length = 10
  Placement = pos=(-15,10,-2) rot=(0,0,1;0rad)
  Width = 2
FEATURE [Part::Box] Box180  label="Re-level Edge Clip Block006"
  AttacherType = Attacher::AttachEngine3D
  Height = 10
  Length = 20
  Placement = pos=(-19,-2,3) rot=(0,0,1;0rad)
  Width = 44
FEATURE [Part::Box] Box181  label="Cube157"
  AttacherType = Attacher::AttachEngine3D
  Height = 7
  Length = 4
  Placement = pos=(-6,27.4,-2) rot=(0,0,1;0rad)
  Width = 7.2
FEATURE [Part::Box] Box182  label="Cube158"
  AttacherType = Attacher::AttachEngine3D
  Height = 7
  Length = 4
  Placement = pos=(-6,12,-2) rot=(0,0,1;0rad)
  Width = 1
FEATURE [Part::Sphere] Sphere059
  Angle1 = -90
  Angle2 = 90
  Angle3 = 360
  AttacherType = Attacher::AttachEngine3D
  Placement = pos=(-7.5,6.5,0.5) rot=(0,0,1;0rad)
  Radius = 1.25
FEATURE [Part::Box] Box183  label="Cube159"
  AttacherType = Attacher::AttachEngine3D
  Height = 7
  Length = 10
  Placement = pos=(-15,25.4,-2) rot=(0,0,1;0rad)
  Width = 2
FEATURE [Part::Box] Box184  label="Cube160"
  AttacherType = Attacher::AttachEngine3D
  Height = 7
  Length = 4
  Placement = pos=(-6,36.6,-2) rot=(0,0,1;0rad)
  Width = 1
FEATURE [Part::Sphere] Sphere060
  Angle1 = -90
  Angle2 = 90
  Angle3 = 360
  AttacherType = Attacher::AttachEngine3D
  Placement = pos=(-7.5,34,0.5) rot=(0,0,1;0rad)
  Radius = 1.5
FEATURE [Part::Box] Box185  label="Cube161"
  AttacherType = Attacher::AttachEngine3D
  Height = 7
  Length = 4
  Placement = pos=(-6,24.4,-2) rot=(0,0,1;0rad)
  Width = 1
FEATURE [Part::Box] Box186  label="Cube162"
  AttacherType = Attacher::AttachEngine3D
  Height = 7
  Length = 4
  Placement = pos=(-6,8,-2) rot=(0,0,1;0rad)
  Width = 2
FEATURE [Part::Box] Box187  label="Re-level Edge Clip Block007"
  AttacherType = Attacher::AttachEngine3D
  Height = 10
  Length = 12
  Placement = pos=(-21.5,-2,-7) rot=(0,0,1;0rad)
  Width = 44
FEATURE [Part::Sphere] Sphere061
  Angle1 = -90
  Angle2 = 90
  Angle3 = 360
  AttacherType = Attacher::AttachEngine3D
  Placement = pos=(-7.5,11.5,0.5) rot=(0,0,1;0rad)
  Radius = 1.25
FEATURE [Part::Sphere] Sphere062
  Angle1 = -90
  Angle2 = 90
  Angle3 = 360
  AttacherType = Attacher::AttachEngine3D
  Placement = pos=(-7.5,28,0.5) rot=(0,0,1;0rad)
  Radius = 1.5
FEATURE [Part::Fuse] Fusion066  label="Holes003"
  Base = -> Sphere062
  Tool = -> Sphere060
FEATURE [Part::Box] Box188  label="Cube163"
  AttacherType = Attacher::AttachEngine3D
  Height = 7
  Length = 10
  Placement = pos=(-15,34.6,-2) rot=(0,0,1;0rad)
  Width = 2
FEATURE [Part::Box] Box189  label="Cube164"
  AttacherType = Attacher::AttachEngine3D
  Height = 7
  Length = 4
  Placement = pos=(-6,5,-2) rot=(0,0,1;0rad)
  Width = 1
FEATURE [Part::MultiFuse] Fusion067  label="Extra Holes for Clips003"
  Shapes = -> [Box181,Box182,Box184,Box186,Box185,Box189]
FEATURE [Part::Box] Box190  label="Cube165"
  AttacherType = Attacher::AttachEngine3D
  Height = 7
  Length = 10
  Placement = pos=(-15,6,-2) rot=(0,0,1;0rad)
  Width = 2
FEATURE [Part::MultiFuse] Fusion069
  Shapes = -> [Box178,Box190,Box179,Box183,Box188]
FEATURE [Part::Fuse] Fusion070  label="Bumps003"
  Base = -> Sphere059
  Tool = -> Sphere061
FEATURE [Part::Fuse] Fusion068
  Base = -> Fusion070
  Tool = -> Fusion069
FEATURE [Part::Cut] Cut073
  Base = -> Fusion068
  Tool = -> Fusion066
FEATURE [Part::Cut] Cut070
  Base = -> Cut073
  Tool = -> Fusion067
FEATURE [Part::Cut] Cut071
  Base = -> Cut070
  Tool = -> Box180
FEATURE [Part::Cut] Cut072
  Base = -> Cut071
  Tool = -> Box187
FEATURE [Part::Box] Box191  label="Chamfer Cube003"
  AttacherType = Attacher::AttachEngine3D
  Height = 10
  Length = 13
  Placement = pos=(-11.69,0,-1.19) rot=(0,-1,0;0.785398rad)
  Width = 40
FEATURE [Part::Cut] Cut074  label="Edge Clips002"
  Base = -> Cut072
  Placement = pos=(20,20,0) rot=(0,0,1;3.14159rad)
  Tool = -> Box191
FEATURE [Part::Box] Box192  label="Cube166"
  AttacherType = Attacher::AttachEngine3D
  Height = 7
  Length = 10
  Placement = pos=(-15,6,-2) rot=(0,0,1;0rad)
  Width = 2
FEATURE [Part::Box] Box193  label="Chamfer Cube004"
  AttacherType = Attacher::AttachEngine3D
  Height = 10
  Length = 13
  Placement = pos=(-11.69,0,-1.19) rot=(0,-1,0;0.785398rad)
  Width = 40
FEATURE [Part::Box] Box194  label="Re-level Edge Clip Block008"
  AttacherType = Attacher::AttachEngine3D
  Height = 10
  Length = 20
  Placement = pos=(-19,-2,3) rot=(0,0,1;0rad)
  Width = 44
FEATURE [Part::Box] Box195  label="Cube167"
  AttacherType = Attacher::AttachEngine3D
  Height = 7
  Length = 10
  Placement = pos=(-15,10,-2) rot=(0,0,1;0rad)
  Width = 2
FEATURE [Part::Box] Box196  label="Cube168"
  AttacherType = Attacher::AttachEngine3D
  Height = 7
  Length = 5
  Placement = pos=(-5,0,-2) rot=(0,0,1;0rad)
  Width = 40
FEATURE [Part::Box] Box197  label="Cube169"
  AttacherType = Attacher::AttachEngine3D
  Height = 7
  Length = 4
  Placement = pos=(-6,5,-2) rot=(0,0,1;0rad)
  Width = 1
FEATURE [Part::Box] Box198  label="Cube170"
  AttacherType = Attacher::AttachEngine3D
  Height = 7
  Length = 4
  Placement = pos=(-6,12,-2) rot=(0,0,1;0rad)
  Width = 1
FEATURE [Part::Box] Box199  label="Cube171"
  AttacherType = Attacher::AttachEngine3D
  Height = 7
  Length = 4
  Placement = pos=(-6,27.4,-2) rot=(0,0,1;0rad)
  Width = 7.2
FEATURE [Part::Box] Box200  label="Cube172"
  AttacherType = Attacher::AttachEngine3D
  Height = 7
  Length = 4
  Placement = pos=(-6,24.4,-2) rot=(0,0,1;0rad)
  Width = 1
FEATURE [Part::Sphere] Sphere063
  Angle1 = -90
  Angle2 = 90
  Angle3 = 360
  AttacherType = Attacher::AttachEngine3D
  Placement = pos=(-7.5,28,0.5) rot=(0,0,1;0rad)
  Radius = 1.5
FEATURE [Part::Sphere] Sphere064
  Angle1 = -90
  Angle2 = 90
  Angle3 = 360
  AttacherType = Attacher::AttachEngine3D
  Placement = pos=(-7.5,11.5,0.5) rot=(0,0,1;0rad)
  Radius = 1.25
FEATURE [Part::Box] Box201  label="Cube173"
  AttacherType = Attacher::AttachEngine3D
  Height = 7
  Length = 4
  Placement = pos=(-6,8,-2) rot=(0,0,1;0rad)
  Width = 2
FEATURE [Part::Box] Box202  label="Cube174"
  AttacherType = Attacher::AttachEngine3D
  Height = 7
  Length = 10
  Placement = pos=(-15,25.4,-2) rot=(0,0,1;0rad)
  Width = 2
FEATURE [Part::Sphere] Sphere065
  Angle1 = -90
  Angle2 = 90
  Angle3 = 360
  AttacherType = Attacher::AttachEngine3D
  Placement = pos=(-7.5,6.5,0.5) rot=(0,0,1;0rad)
  Radius = 1.25
FEATURE [Part::Fuse] Fusion073  label="Bumps004"
  Base = -> Sphere065
  Tool = -> Sphere064
FEATURE [Part::Sphere] Sphere066
  Angle1 = -90
  Angle2 = 90
  Angle3 = 360
  AttacherType = Attacher::AttachEngine3D
  Placement = pos=(-7.5,34,0.5) rot=(0,0,1;0rad)
  Radius = 1.5
FEATURE [Part::Fuse] Fusion071  label="Holes004"
  Base = -> Sphere063
  Tool = -> Sphere066
FEATURE [Part::Box] Box203  label="Re-level Edge Clip Block009"
  AttacherType = Attacher::AttachEngine3D
  Height = 10
  Length = 12
  Placement = pos=(-21.5,-2,-7) rot=(0,0,1;0rad)
  Width = 44
FEATURE [Part::Box] Box204  label="Cube175"
  AttacherType = Attacher::AttachEngine3D
  Height = 7
  Length = 4
  Placement = pos=(-6,36.6,-2) rot=(0,0,1;0rad)
  Width = 1
FEATURE [Part::MultiFuse] Fusion074  label="Extra Holes for Clips004"
  Shapes = -> [Box199,Box198,Box204,Box201,Box200,Box197]
FEATURE [Part::Box] Box205  label="Cube176"
  AttacherType = Attacher::AttachEngine3D
  Height = 7
  Length = 10
  Placement = pos=(-15,34.6,-2) rot=(0,0,1;0rad)
  Width = 2
FEATURE [Part::MultiFuse] Fusion072
  Shapes = -> [Box196,Box192,Box195,Box202,Box205]
FEATURE [Part::Fuse] Fusion075
  Base = -> Fusion073
  Tool = -> Fusion072
FEATURE [Part::Cut] Cut075
  Base = -> Fusion075
  Tool = -> Fusion071
FEATURE [Part::Cut] Cut076
  Base = -> Cut075
  Tool = -> Fusion074
FEATURE [Part::Cut] Cut078
  Base = -> Cut076
  Tool = -> Box194
FEATURE [Part::Cut] Cut077
  Base = -> Cut078
  Tool = -> Box203
FEATURE [Part::Cut] Cut079  label="Edge Clips003"
  Base = -> Cut077
  Placement = pos=(-20,20,0) rot=(0,0,-1;1.5708rad)
  Tool = -> Box193
FEATURE [Part::MultiFuse] Fusion076  label="Edge Clips Fusion"
  Shapes = -> [Cut059,Cut069,Cut074,Cut079]
FEATURE [Part::Box] Box206  label="Cube177"
  AttacherType = Attacher::AttachEngine3D
  Height = 10
  Length = 10
  Placement = pos=(26,4,1) rot=(0.442189,-0.287968,0.849437;1.66134rad)
  Width = 15
FEATURE [Part::Box] Box207  label="Cube178"
  AttacherType = Attacher::AttachEngine3D
  Height = 10
  Length = 10
  Placement = pos=(-4,26,1) rot=(0.381439,0.080566,0.920876;3.07487rad)
  Width = 15
FEATURE [Part::Box] Box208  label="Cube179"
  AttacherType = Attacher::AttachEngine3D
  Height = 10
  Length = 10
  Placement = pos=(-26,-4,1) rot=(-0.273007,-0.419215,-0.865867;1.78566rad)
  Width = 15
FEATURE [Part::MultiFuse] Fusion078  label="Glue Dents"
  Shapes = -> [Box086,Box208,Box207,Box206]
FEATURE [Part::Box] Box209  label="Cube180"
  AttacherType = Attacher::AttachEngine3D
  Height = 7
  Length = 5
  Placement = pos=(-5,0,-2) rot=(0,0,1;0rad)
  Width = 40
FEATURE [Part::Box] Box210  label="Cube181"
  AttacherType = Attacher::AttachEngine3D
  Height = 7
  Length = 10
  Placement = pos=(-15,6,-2) rot=(0,0,1;0rad)
  Width = 2
FEATURE [Part::Box] Box211  label="Cube182"
  AttacherType = Attacher::AttachEngine3D
  Height = 7
  Length = 10
  Placement = pos=(-15,10,-2) rot=(0,0,1;0rad)
  Width = 2
FEATURE [Part::Box] Box212  label="Cube183"
  AttacherType = Attacher::AttachEngine3D
  Height = 7
  Length = 10
  Placement = pos=(-15,25.4,-2) rot=(0,0,1;0rad)
  Width = 2
FEATURE [Part::Box] Box213  label="Cube184"
  AttacherType = Attacher::AttachEngine3D
  Height = 7
  Length = 10
  Placement = pos=(-15,34.6,-2) rot=(0,0,1;0rad)
  Width = 2
FEATURE [Part::Sphere] Sphere067
  Angle1 = -90
  Angle2 = 90
  Angle3 = 360
  AttacherType = Attacher::AttachEngine3D
  Placement = pos=(-7.5,6.5,0.5) rot=(0,0,1;0rad)
  Radius = 1.25
FEATURE [Part::Box] Box214  label="Chamfer Cube005"
  AttacherType = Attacher::AttachEngine3D
  Height = 10
  Length = 13
  Placement = pos=(-11.69,0,-1.19) rot=(0,-1,0;0.785398rad)
  Width = 40
FEATURE [Part::Sphere] Sphere068
  Angle1 = -90
  Angle2 = 90
  Angle3 = 360
  AttacherType = Attacher::AttachEngine3D
  Placement = pos=(-7.5,11.5,0.5) rot=(0,0,1;0rad)
  Radius = 1.25
FEATURE [Part::Sphere] Sphere069
  Angle1 = -90
  Angle2 = 90
  Angle3 = 360
  AttacherType = Attacher::AttachEngine3D
  Placement = pos=(-7.5,28,0.5) rot=(0,0,1;0rad)
  Radius = 1.5
FEATURE [Part::Sphere] Sphere070
  Angle1 = -90
  Angle2 = 90
  Angle3 = 360
  AttacherType = Attacher::AttachEngine3D
  Placement = pos=(-7.5,34,0.5) rot=(0,0,1;0rad)
  Radius = 1.5
FEATURE [Part::Box] Box215  label="Cube185"
  AttacherType = Attacher::AttachEngine3D
  Height = 7
  Length = 4
  Placement = pos=(-6,5,-2) rot=(0,0,1;0rad)
  Width = 1
FEATURE [Part::Box] Box216  label="Cube186"
  AttacherType = Attacher::AttachEngine3D
  Height = 7
  Length = 4
  Placement = pos=(-6,8,-2) rot=(0,0,1;0rad)
  Width = 2
FEATURE [Part::Box] Box217  label="Cube187"
  AttacherType = Attacher::AttachEngine3D
  Height = 7
  Length = 4
  Placement = pos=(-6,12,-2) rot=(0,0,1;0rad)
  Width = 1
FEATURE [Part::Box] Box218  label="Cube188"
  AttacherType = Attacher::AttachEngine3D
  Height = 7
  Length = 4
  Placement = pos=(-6,24.4,-2) rot=(0,0,1;0rad)
  Width = 1
FEATURE [Part::Box] Box219  label="Cube189"
  AttacherType = Attacher::AttachEngine3D
  Height = 7
  Length = 4
  Placement = pos=(-6,36.6,-2) rot=(0,0,1;0rad)
  Width = 1
FEATURE [Part::Box] Box220  label="Cube190"
  AttacherType = Attacher::AttachEngine3D
  Height = 7
  Length = 4
  Placement = pos=(-6,27.4,-2) rot=(0,0,1;0rad)
  Width = 7.2
FEATURE [Part::MultiFuse] Fusion079  label="Extra Holes for Clips005"
  Shapes = -> [Box220,Box217,Box219,Box216,Box218,Box215]
FEATURE [Part::Box] Box221  label="Re-level Edge Clip Block010"
  AttacherType = Attacher::AttachEngine3D
  Height = 10
  Length = 20
  Placement = pos=(-19,-2,3) rot=(0,0,1;0rad)
  Width = 44
FEATURE [Part::Box] Box222  label="Re-level Edge Clip Block011"
  AttacherType = Attacher::AttachEngine3D
  Height = 10
  Length = 12
  Placement = pos=(-21.5,-2,-7) rot=(0,0,1;0rad)
  Width = 44
FEATURE [Part::Fuse] Fusion080  label="Bumps005"
  Base = -> Sphere067
  Tool = -> Sphere068
FEATURE [Part::Fuse] Fusion081  label="Holes005"
  Base = -> Sphere069
  Tool = -> Sphere070
FEATURE [Part::MultiFuse] Fusion082
  Shapes = -> [Box209,Box210,Box211,Box212,Box213]
FEATURE [Part::Fuse] Fusion083
  Base = -> Fusion080
  Tool = -> Fusion082
FEATURE [Part::Cut] Cut082
  Base = -> Fusion083
  Tool = -> Fusion081
FEATURE [Part::Cut] Cut083
  Base = -> Cut082
  Tool = -> Fusion079
FEATURE [Part::Cut] Cut084
  Base = -> Cut083
  Tool = -> Box221
FEATURE [Part::Cut] Cut085
  Base = -> Cut084
  Tool = -> Box222
FEATURE [Part::Cut] Cut086  label="Edge Clips Master001"
  Base = -> Cut085
  Placement = pos=(-20,-20,0) rot=(0,0,1;0rad)
  Tool = -> Box214
FEATURE [Part::Box] Box223  label="Cube191"
  AttacherType = Attacher::AttachEngine3D
  Height = 7
  Length = 5
  Placement = pos=(-5,0,-2) rot=(0,0,1;0rad)
  Width = 40
FEATURE [Part::Box] Box224  label="Cube192"
  AttacherType = Attacher::AttachEngine3D
  Height = 7
  Length = 4
  Placement = pos=(-6,8,-2) rot=(0,0,1;0rad)
  Width = 2
FEATURE [Part::Box] Box225  label="Chamfer Cube006"
  AttacherType = Attacher::AttachEngine3D
  Height = 10
  Length = 13
  Placement = pos=(-11.69,0,-1.19) rot=(0,-1,0;0.785398rad)
  Width = 40
FEATURE [Part::Box] Box226  label="Cube193"
  AttacherType = Attacher::AttachEngine3D
  Height = 7
  Length = 10
  Placement = pos=(-15,6,-2) rot=(0,0,1;0rad)
  Width = 2
FEATURE [Part::Sphere] Sphere071
  Angle1 = -90
  Angle2 = 90
  Angle3 = 360
  AttacherType = Attacher::AttachEngine3D
  Placement = pos=(-7.5,11.5,0.5) rot=(0,0,1;0rad)
  Radius = 1.25
FEATURE [Part::Box] Box227  label="Cube194"
  AttacherType = Attacher::AttachEngine3D
  Height = 7
  Length = 4
  Placement = pos=(-6,27.4,-2) rot=(0,0,1;0rad)
  Width = 7.2
FEATURE [Part::Box] Box228  label="Cube195"
  AttacherType = Attacher::AttachEngine3D
  Height = 7
  Length = 4
  Placement = pos=(-6,12,-2) rot=(0,0,1;0rad)
  Width = 1
FEATURE [Part::Box] Box229  label="Cube196"
  AttacherType = Attacher::AttachEngine3D
  Height = 7
  Length = 4
  Placement = pos=(-6,24.4,-2) rot=(0,0,1;0rad)
  Width = 1
FEATURE [Part::Sphere] Sphere072
  Angle1 = -90
  Angle2 = 90
  Angle3 = 360
  AttacherType = Attacher::AttachEngine3D
  Placement = pos=(-7.5,6.5,0.5) rot=(0,0,1;0rad)
  Radius = 1.25
FEATURE [Part::Box] Box230  label="Cube197"
  AttacherType = Attacher::AttachEngine3D
  Height = 7
  Length = 4
  Placement = pos=(-6,36.6,-2) rot=(0,0,1;0rad)
  Width = 1
FEATURE [Part::Box] Box231  label="Cube198"
  AttacherType = Attacher::AttachEngine3D
  Height = 7
  Length = 10
  Placement = pos=(-15,10,-2) rot=(0,0,1;0rad)
  Width = 2
FEATURE [Part::Sphere] Sphere073
  Angle1 = -90
  Angle2 = 90
  Angle3 = 360
  AttacherType = Attacher::AttachEngine3D
  Placement = pos=(-7.5,34,0.5) rot=(0,0,1;0rad)
  Radius = 1.5
FEATURE [Part::Box] Box232  label="Cube199"
  AttacherType = Attacher::AttachEngine3D
  Height = 7
  Length = 4
  Placement = pos=(-6,5,-2) rot=(0,0,1;0rad)
  Width = 1
FEATURE [Part::MultiFuse] Fusion085  label="Extra Holes for Clips006"
  Shapes = -> [Box227,Box228,Box230,Box224,Box229,Box232]
FEATURE [Part::Box] Box233  label="Re-level Edge Clip Block012"
  AttacherType = Attacher::AttachEngine3D
  Height = 10
  Length = 20
  Placement = pos=(-19,-2,3) rot=(0,0,1;0rad)
  Width = 44
FEATURE [Part::Box] Box234  label="Cube200"
  AttacherType = Attacher::AttachEngine3D
  Height = 7
  Length = 10
  Placement = pos=(-15,34.6,-2) rot=(0,0,1;0rad)
  Width = 2
FEATURE [Part::Box] Box235  label="Cube201"
  AttacherType = Attacher::AttachEngine3D
  Height = 7
  Length = 10
  Placement = pos=(-15,25.4,-2) rot=(0,0,1;0rad)
  Width = 2
FEATURE [Part::MultiFuse] Fusion086
  Shapes = -> [Box223,Box226,Box231,Box235,Box234]
FEATURE [Part::Fuse] Fusion087  label="Bumps006"
  Base = -> Sphere072
  Tool = -> Sphere071
FEATURE [Part::Fuse] Fusion084
  Base = -> Fusion087
  Tool = -> Fusion086
FEATURE [Part::Sphere] Sphere074
  Angle1 = -90
  Angle2 = 90
  Angle3 = 360
  AttacherType = Attacher::AttachEngine3D
  Placement = pos=(-7.5,28,0.5) rot=(0,0,1;0rad)
  Radius = 1.5
FEATURE [Part::Fuse] Fusion088  label="Holes006"
  Base = -> Sphere074
  Tool = -> Sphere073
FEATURE [Part::Box] Box236  label="Re-level Edge Clip Block013"
  AttacherType = Attacher::AttachEngine3D
  Height = 10
  Length = 12
  Placement = pos=(-21.5,-2,-7) rot=(0,0,1;0rad)
  Width = 44
FEATURE [Part::Cut] Cut087
  Base = -> Fusion084
  Tool = -> Fusion088
FEATURE [Part::Cut] Cut088
  Base = -> Cut087
  Tool = -> Fusion085
FEATURE [Part::Cut] Cut089
  Base = -> Cut088
  Tool = -> Box233
FEATURE [Part::Cut] Cut090
  Base = -> Cut089
  Tool = -> Box236
FEATURE [Part::Cut] Cut091  label="Edge Clips004"
  Base = -> Cut090
  Placement = pos=(20,-20,0) rot=(0,0,1;1.5708rad)
  Tool = -> Box225
FEATURE [Part::Box] Box237  label="Re-level Edge Clip Block014"
  AttacherType = Attacher::AttachEngine3D
  Height = 10
  Length = 12
  Placement = pos=(-21.5,-2,-7) rot=(0,0,1;0rad)
  Width = 44
FEATURE [Part::Box] Box238  label="Cube202"
  AttacherType = Attacher::AttachEngine3D
  Height = 7
  Length = 4
  Placement = pos=(-6,36.6,-2) rot=(0,0,1;0rad)
  Width = 1
FEATURE [Part::Box] Box239  label="Cube203"
  AttacherType = Attacher::AttachEngine3D
  Height = 7
  Length = 10
  Placement = pos=(-15,10,-2) rot=(0,0,1;0rad)
  Width = 2
FEATURE [Part::Box] Box240  label="Cube204"
  AttacherType = Attacher::AttachEngine3D
  Height = 7
  Length = 10
  Placement = pos=(-15,25.4,-2) rot=(0,0,1;0rad)
  Width = 2
FEATURE [Part::Box] Box241  label="Re-level Edge Clip Block015"
  AttacherType = Attacher::AttachEngine3D
  Height = 10
  Length = 20
  Placement = pos=(-19,-2,3) rot=(0,0,1;0rad)
  Width = 44
FEATURE [Part::Box] Box242  label="Cube205"
  AttacherType = Attacher::AttachEngine3D
  Height = 7
  Length = 10
  Placement = pos=(-15,34.6,-2) rot=(0,0,1;0rad)
  Width = 2
FEATURE [Part::Sphere] Sphere075
  Angle1 = -90
  Angle2 = 90
  Angle3 = 360
  AttacherType = Attacher::AttachEngine3D
  Placement = pos=(-7.5,34,0.5) rot=(0,0,1;0rad)
  Radius = 1.5
FEATURE [Part::Sphere] Sphere076
  Angle1 = -90
  Angle2 = 90
  Angle3 = 360
  AttacherType = Attacher::AttachEngine3D
  Placement = pos=(-7.5,28,0.5) rot=(0,0,1;0rad)
  Radius = 1.5
FEATURE [Part::Fuse] Fusion089  label="Holes007"
  Base = -> Sphere076
  Tool = -> Sphere075
FEATURE [Part::Box] Box243  label="Cube206"
  AttacherType = Attacher::AttachEngine3D
  Height = 7
  Length = 4
  Placement = pos=(-6,5,-2) rot=(0,0,1;0rad)
  Width = 1
FEATURE [Part::Box] Box244  label="Cube207"
  AttacherType = Attacher::AttachEngine3D
  Height = 7
  Length = 4
  Placement = pos=(-6,24.4,-2) rot=(0,0,1;0rad)
  Width = 1
FEATURE [Part::Sphere] Sphere077
  Angle1 = -90
  Angle2 = 90
  Angle3 = 360
  AttacherType = Attacher::AttachEngine3D
  Placement = pos=(-7.5,11.5,0.5) rot=(0,0,1;0rad)
  Radius = 1.25
FEATURE [Part::Box] Box245  label="Cube208"
  AttacherType = Attacher::AttachEngine3D
  Height = 7
  Length = 4
  Placement = pos=(-6,12,-2) rot=(0,0,1;0rad)
  Width = 1
FEATURE [Part::Box] Box246  label="Chamfer Cube007"
  AttacherType = Attacher::AttachEngine3D
  Height = 10
  Length = 13
  Placement = pos=(-11.69,0,-1.19) rot=(0,-1,0;0.785398rad)
  Width = 40
FEATURE [Part::Sphere] Sphere078
  Angle1 = -90
  Angle2 = 90
  Angle3 = 360
  AttacherType = Attacher::AttachEngine3D
  Placement = pos=(-7.5,6.5,0.5) rot=(0,0,1;0rad)
  Radius = 1.25
FEATURE [Part::Fuse] Fusion090  label="Bumps007"
  Base = -> Sphere078
  Tool = -> Sphere077
FEATURE [Part::Box] Box247  label="Cube209"
  AttacherType = Attacher::AttachEngine3D
  Height = 7
  Length = 5
  Placement = pos=(-5,0,-2) rot=(0,0,1;0rad)
  Width = 40
FEATURE [Part::Box] Box248  label="Cube210"
  AttacherType = Attacher::AttachEngine3D
  Height = 7
  Length = 4
  Placement = pos=(-6,27.4,-2) rot=(0,0,1;0rad)
  Width = 7.2
FEATURE [Part::Box] Box249  label="Cube211"
  AttacherType = Attacher::AttachEngine3D
  Height = 7
  Length = 4
  Placement = pos=(-6,8,-2) rot=(0,0,1;0rad)
  Width = 2
FEATURE [Part::MultiFuse] Fusion091  label="Extra Holes for Clips007"
  Shapes = -> [Box248,Box245,Box238,Box249,Box244,Box243]
FEATURE [Part::Box] Box250  label="Cube212"
  AttacherType = Attacher::AttachEngine3D
  Height = 7
  Length = 10
  Placement = pos=(-15,6,-2) rot=(0,0,1;0rad)
  Width = 2
FEATURE [Part::MultiFuse] Fusion092
  Shapes = -> [Box247,Box250,Box239,Box240,Box242]
FEATURE [Part::Fuse] Fusion093
  Base = -> Fusion090
  Tool = -> Fusion092
FEATURE [Part::Cut] Cut093
  Base = -> Fusion093
  Tool = -> Fusion089
FEATURE [Part::Cut] Cut094
  Base = -> Cut093
  Tool = -> Fusion091
FEATURE [Part::Cut] Cut095
  Base = -> Cut094
  Tool = -> Box241
FEATURE [Part::Cut] Cut096
  Base = -> Cut095
  Tool = -> Box237
FEATURE [Part::Cut] Cut092  label="Edge Clips005"
  Base = -> Cut096
  Placement = pos=(20,20,0) rot=(0,0,1;3.14159rad)
  Tool = -> Box246
FEATURE [Part::Box] Box251  label="Re-level Edge Clip Block016"
  AttacherType = Attacher::AttachEngine3D
  Height = 10
  Length = 12
  Placement = pos=(-21.5,-2,-7) rot=(0,0,1;0rad)
  Width = 44
FEATURE [Part::Box] Box252  label="Cube213"
  AttacherType = Attacher::AttachEngine3D
  Height = 7
  Length = 10
  Placement = pos=(-15,10,-2) rot=(0,0,1;0rad)
  Width = 2
FEATURE [Part::Box] Box253  label="Cube214"
  AttacherType = Attacher::AttachEngine3D
  Height = 7
  Length = 4
  Placement = pos=(-6,12,-2) rot=(0,0,1;0rad)
  Width = 1
FEATURE [Part::Box] Box254  label="Chamfer Cube008"
  AttacherType = Attacher::AttachEngine3D
  Height = 10
  Length = 13
  Placement = pos=(-11.69,0,-1.19) rot=(0,-1,0;0.785398rad)
  Width = 40
FEATURE [Part::Sphere] Sphere079
  Angle1 = -90
  Angle2 = 90
  Angle3 = 360
  AttacherType = Attacher::AttachEngine3D
  Placement = pos=(-7.5,6.5,0.5) rot=(0,0,1;0rad)
  Radius = 1.25
FEATURE [Part::Box] Box255  label="Cube215"
  AttacherType = Attacher::AttachEngine3D
  Height = 7
  Length = 5
  Placement = pos=(-5,0,-2) rot=(0,0,1;0rad)
  Width = 40
FEATURE [Part::Box] Box256  label="Cube216"
  AttacherType = Attacher::AttachEngine3D
  Height = 7
  Length = 4
  Placement = pos=(-6,27.4,-2) rot=(0,0,1;0rad)
  Width = 7.2
FEATURE [Part::Box] Box257  label="Cube217"
  AttacherType = Attacher::AttachEngine3D
  Height = 7
  Length = 4
  Placement = pos=(-6,8,-2) rot=(0,0,1;0rad)
  Width = 2
FEATURE [Part::Box] Box258  label="Cube218"
  AttacherType = Attacher::AttachEngine3D
  Height = 7
  Length = 10
  Placement = pos=(-15,6,-2) rot=(0,0,1;0rad)
  Width = 2
FEATURE [Part::Sphere] Sphere080
  Angle1 = -90
  Angle2 = 90
  Angle3 = 360
  AttacherType = Attacher::AttachEngine3D
  Placement = pos=(-7.5,28,0.5) rot=(0,0,1;0rad)
  Radius = 1.5
FEATURE [Part::Box] Box259  label="Cube219"
  AttacherType = Attacher::AttachEngine3D
  Height = 7
  Length = 4
  Placement = pos=(-6,5,-2) rot=(0,0,1;0rad)
  Width = 1
FEATURE [Part::Box] Box260  label="Cube220"
  AttacherType = Attacher::AttachEngine3D
  Height = 7
  Length = 4
  Placement = pos=(-6,24.4,-2) rot=(0,0,1;0rad)
  Width = 1
FEATURE [Part::Sphere] Sphere081
  Angle1 = -90
  Angle2 = 90
  Angle3 = 360
  AttacherType = Attacher::AttachEngine3D
  Placement = pos=(-7.5,11.5,0.5) rot=(0,0,1;0rad)
  Radius = 1.25
FEATURE [Part::Box] Box261  label="Re-level Edge Clip Block017"
  AttacherType = Attacher::AttachEngine3D
  Height = 10
  Length = 20
  Placement = pos=(-19,-2,3) rot=(0,0,1;0rad)
  Width = 44
FEATURE [Part::Box] Box262  label="Cube221"
  AttacherType = Attacher::AttachEngine3D
  Height = 7
  Length = 10
  Placement = pos=(-15,34.6,-2) rot=(0,0,1;0rad)
  Width = 2
FEATURE [Part::Box] Box263  label="Cube222"
  AttacherType = Attacher::AttachEngine3D
  Height = 7
  Length = 10
  Placement = pos=(-15,25.4,-2) rot=(0,0,1;0rad)
  Width = 2
FEATURE [Part::MultiFuse] Fusion096
  Shapes = -> [Box255,Box258,Box252,Box263,Box262]
FEATURE [Part::Box] Box264  label="Cube223"
  AttacherType = Attacher::AttachEngine3D
  Height = 7
  Length = 4
  Placement = pos=(-6,36.6,-2) rot=(0,0,1;0rad)
  Width = 1
FEATURE [Part::MultiFuse] Fusion095  label="Extra Holes for Clips008"
  Shapes = -> [Box256,Box253,Box264,Box257,Box260,Box259]
FEATURE [Part::Fuse] Fusion098  label="Bumps008"
  Base = -> Sphere079
  Tool = -> Sphere081
FEATURE [Part::Fuse] Fusion094
  Base = -> Fusion098
  Tool = -> Fusion096
FEATURE [Part::Sphere] Sphere082
  Angle1 = -90
  Angle2 = 90
  Angle3 = 360
  AttacherType = Attacher::AttachEngine3D
  Placement = pos=(-7.5,34,0.5) rot=(0,0,1;0rad)
  Radius = 1.5
FEATURE [Part::Fuse] Fusion097  label="Holes008"
  Base = -> Sphere080
  Tool = -> Sphere082
FEATURE [Part::Cut] Cut101
  Base = -> Fusion094
  Tool = -> Fusion097
FEATURE [Part::Cut] Cut097
  Base = -> Cut101
  Tool = -> Fusion095
FEATURE [Part::Cut] Cut098
  Base = -> Cut097
  Tool = -> Box261
FEATURE [Part::Cut] Cut099
  Base = -> Cut098
  Tool = -> Box251
FEATURE [Part::Cut] Cut100  label="Edge Clips006"
  Base = -> Cut099
  Placement = pos=(-20,20,0) rot=(0,0,-1;1.5708rad)
  Tool = -> Box254
FEATURE [Part::Box] Box265  label="Cube224"
  AttacherType = Attacher::AttachEngine3D
  Height = 10
  Length = 10
  Placement = pos=(4,-26,1) rot=(0.205904,-0.974848,-0.085288;0.803573rad)
  Width = 15
FEATURE [Part::Box] Box266  label="Cube225"
  AttacherType = Attacher::AttachEngine3D
  Height = 10
  Length = 10
  Placement = pos=(-26,-4,1) rot=(-0.273007,-0.419215,-0.865867;1.78566rad)
  Width = 15
FEATURE [Part::Box] Box267  label="Cube226"
  AttacherType = Attacher::AttachEngine3D
  Height = 10
  Length = 10
  Placement = pos=(-4,26,1) rot=(0.381439,0.080566,0.920876;3.07487rad)
  Width = 15
FEATURE [Part::Box] Box268  label="Cube227"
  AttacherType = Attacher::AttachEngine3D
  Height = 10
  Length = 10
  Placement = pos=(26,4,1) rot=(0.442189,-0.287968,0.849437;1.66134rad)
  Width = 15
FEATURE [Part::MultiFuse] Fusion099  label="Glue Dents001"
  Shapes = -> [Box265,Box266,Box267,Box268]
FEATURE [Part::MultiFuse] Fusion100  label="Edge Clips Fusion001"
  Shapes = -> [Cut100,Cut086,Cut091,Cut092]
FEATURE [Drawing::FeatureViewAnnotation] Annotation001
  Font = Sans
  Rotation = 0
  Scale = 7
  Text = 0.5 rejigged whole thing, stopped clips overhang and moved bump and holes back 0.5
  ViewResult = <g transform="translate(14,30) rotate(0)">\n<text id="Annotation001"\n font-family="Sans"\n font-size="7"\n fill="#000000">\n<tspan x="0" dy="1em">0.5 rejigged whole thing, stopped clips overhang and moved bump and holes back 0.5</tspan>\n</text>\n</g>
  Visible = false
  X = 14
  Y = 30
FEATURE [Part::Cylinder] Cylinder027
  Angle = 360
  AttacherType = Attacher::AttachEngine3D
  Height = 73
  Placement = pos=(0,0,-50) rot=(0,0,1;0rad)
  Radius = 0.5
FEATURE [Part::MultiFuse] Fusion101
  Placement = pos=(-15,-15,0) rot=(0,0,1;0rad)
  Shapes = -> [Box069,Cylinder018,Sphere030]
FEATURE [App::DocumentObjectGroup] Group002  label="Old 0.1"
  Group = -> [Sphere027,Sphere028,Sphere029,Sphere031,Sphere032,Sphere033,Sphere034,Cylinder012,Cylinder016,Cylinder015,Cylinder014,Cylinder013,Cylinder017,Cylinder019,Box067,Box073,Box071,Box068,Box070,Box072,Box074]
FEATURE [Part::Box] Box269  label="Square Nut Hole 024"
  AttacherType = Attacher::AttachEngine3D
  Height = 2
  Length = 5.8
  Placement = pos=(-2.9,2.9,2.1) rot=(1,0,0;3.14159rad)
  Width = 5.8
FEATURE [Part::Cylinder] Cylinder028
  Angle = 360
  AttacherType = Attacher::AttachEngine3D
  Height = 10
  Placement = pos=(0,0,6.7) rot=(1,0,0;3.14159rad)
  Radius = 1.7
FEATURE [Part::Sphere] Sphere083
  Angle1 = -90
  Angle2 = 90
  Angle3 = 360
  AttacherType = Attacher::AttachEngine3D
  Placement = pos=(0,0,4.3) rot=(1,0,0;3.14159rad)
  Radius = 3.35
FEATURE [Part::MultiFuse] Fusion102
  Placement = pos=(-15,0,0) rot=(0,0,1;0rad)
  Shapes = -> [Box269,Cylinder028,Sphere083]
FEATURE [Part::Fuse] Fusion103
  Base = -> Fusion101
  Tool = -> Fusion102
FEATURE [Part::Feature] Fusion103001
  Placement = pos=(0,0,0) rot=(0,0,1;1.5708rad)
  shape: bbox 21.7 x 6.7 x 10.95 mm, 18 faces, 2 solids (baked)
FEATURE [Part::Feature] Fusion103002
  Placement = pos=(0,0,0) rot=(0,0,1;3.14159rad)
  shape: bbox 6.7 x 21.7 x 10.95 mm, 18 faces, 2 solids (baked)
FEATURE [Part::Feature] Fusion103003
  Placement = pos=(0,0,0) rot=(0,0,-1;1.5708rad)
  shape: bbox 21.7 x 6.7 x 10.95 mm, 18 faces, 2 solids (baked)
FEATURE [Part::MultiFuse] Fusion103004  label="Nut Holes"
  Shapes = -> [Fusion103,Fusion103001,Fusion103002,Fusion103003]
FEATURE [Part::Fuse] Fusion103005  label="Cube with Edge Clips"
  Base = -> Box075
  Tool = -> Fusion100
FEATURE [Part::Cut] Cut102
  Base = -> Fusion103005
  Tool = -> Fusion099
FEATURE [Part::Cut] Cut103
  Base = -> Cut102
  Tool = -> Fusion103004
FEATURE [Part::Cut] Cut104
  Base = -> Cut103
  Tool = -> Chamfer014
FEATURE [Part::Cut] Cut105
  Base = -> Cut104
  Tool = -> Chamfer013
FEATURE [Part::Cut] Cut106  label="Nut Plate 1.1"
  Base = -> Cut105
  Tool = -> Box145
FEATURE [Part::Fuse] Fusion103006
  Base = -> Cut047
  Tool = -> Fusion076
FEATURE [Part::Cut] Cut107
  Base = -> Fusion103006
  Tool = -> Fusion052
FEATURE [Part::Cut] Cut108
  Base = -> Cut107
  Tool = -> Chamfer008
FEATURE [Part::Cut] Cut109
  Base = -> Cut108
  Tool = -> Box085
FEATURE [Part::Cut] Cut110  label="Ball Plate 1.1"
  Base = -> Cut109
  Tool = -> Fusion078
FEATURE [Drawing::FeatureViewAnnotation] Annotation002
  Font = Sans
  Rotation = 0
  Scale = 7
  ViewResult = <g transform="translate(10,10) rotate(0)">\n<text id="Annotation002"\n font-family="Sans"\n font-size="7"\n fill="#000000">\n<tspan x="0" dy="1em"></tspan>\n</text>\n</g>
  Visible = true
  X = 10
  Y = 10
FEATURE [Drawing::FeatureViewAnnotation] Annotation003
  Font = Sans
  Rotation = 0
  Scale = 7
  Text = 0.5 - > 1.0
  ViewResult = <g transform="translate(14,18) rotate(0)">\n<text id="Annotation003"\n font-family="Sans"\n font-size="7"\n fill="#000000">\n<tspan x="0" dy="1em">0.5 - > 1.0</tspan>\n</text>\n</g>
  Visible = false
  X = 14
  Y = 18
FEATURE [Drawing::FeatureViewAnnotation] Annotation004
  Font = Sans
  Rotation = 0
  Scale = 7
  ViewResult = <g transform="translate(10,10) rotate(0)">\n<text id="Annotation004"\n font-family="Sans"\n font-size="7"\n fill="#000000">\n<tspan x="0" dy="1em"></tspan>\n</text>\n</g>
  Visible = true
  X = 10
  Y = 10
FEATURE [Drawing::FeaturePage] Page
  EditableTexts = AUTHOR NAME | CREATION DATE | SUPERVISOR NAME | CHECK DATE | SCALE | WEIGHT | NUMBER | SHEET | TITLE | SUBTITLE
  Group = -> [Annotation,Annotation001,Annotation002,Annotation004]
  Template = <path>
FEATURE [Drawing::FeatureViewAnnotation] Annotation005
  Font = Sans
  Rotation = 0
  Scale = 5
  Text = 0.5 is a working version. 1.0 has everything moved to centre point and then the ball and nut holes moved so that blocks can be mounted in half position
  ViewResult = <g transform="translate(10,30) rotate(0)">\n<text id="Annotation005"\n font-family="Sans"\n font-size="5"\n fill="#000000">\n<tspan x="0" dy="1em">0.5 is a working version. 1.0 has everything moved to centre point and then the ball and nut holes moved so that blocks can be mounted in half position</tspan>\n</text>\n</g>
  Visible = false
  X = 10
  Y = 30
FEATURE [Drawing::FeatureViewAnnotation] Annotation006
  Font = Sans
  Rotation = 0
  Scale = 5
  Text = 1.1 Moved the cube creating the hole with the octagon by 1mm to so distance between pcbs is bigger | Also added holes
  ViewResult = <g transform="translate(10,40) rotate(0)">\n<text id="Annotation006"\n font-family="Sans"\n font-size="5"\n fill="#000000">\n<tspan x="0" dy="1em">1.1 Moved the cube creating the hole with the octagon by 1mm to so distance between pcbs is bigger</tspan>\n<tspan x="0" dy="1em">Also added holes</tspan>\n<tspan x="0" dy="1em"></tspan>\n</text>\n</g>
  Visible = false
  X = 10
  Y = 40
FEATURE [Drawing::FeaturePage] Page001
  EditableTexts = AUTHOR NAME | CREATION DATE | SUPERVISOR NAME | CHECK DATE | SCALE | WEIGHT | NUMBER | SHEET | TITLE | SUBTITLE
  Group = -> [Annotation003,Annotation005,Annotation006]
  Template = <path>
FEATURE [Part::Cylinder] Cylinder029
  Angle = 360
  AttacherType = Attacher::AttachEngine3D
  Height = 10
  Placement = pos=(15,-15,-5) rot=(0,0,1;1.5708rad)
  Radius = 1.7
FEATURE [Part::Sphere] Sphere084  label="Mag Hole001"
  Angle1 = -90
  Angle2 = 90
  Angle3 = 360
  AttacherType = Attacher::AttachEngine3D
  Placement = pos=(15,-15,1.7) rot=(0,0,1;1.5708rad)
  Radius = 2.83
FEATURE [Part::Sphere] Sphere085  label="Mag Hole002"
  Angle1 = -90
  Angle2 = 90
  Angle3 = 360
  AttacherType = Attacher::AttachEngine3D
  Placement = pos=(15,15,1.7) rot=(0,0,1;3.14159rad)
  Radius = 2.83
FEATURE [Part::Sphere] Sphere086  label="Mag Hole 004"
  Angle1 = -90
  Angle2 = 90
  Angle3 = 360
  AttacherType = Attacher::AttachEngine3D
  Placement = pos=(0,15,1.7) rot=(0,0,1;1.5708rad)
  Radius = 2.825
FEATURE [Part::Sphere] Sphere087  label="Mag Hole 005"
  Angle1 = -90
  Angle2 = 90
  Angle3 = 360
  AttacherType = Attacher::AttachEngine3D
  Placement = pos=(-15,0,1.7) rot=(0,0,1;3.14159rad)
  Radius = 2.825
FEATURE [Part::Sphere] Sphere088  label="Mag Hole 006"
  Angle1 = -90
  Angle2 = 90
  Angle3 = 360
  AttacherType = Attacher::AttachEngine3D
  Placement = pos=(0,-15,1.7) rot=(0,0,1;4.71239rad)
  Radius = 2.825
FEATURE [Part::Cylinder] Cylinder030
  Angle = 360
  AttacherType = Attacher::AttachEngine3D
  Height = 10
  Placement = pos=(15,15,-5) rot=(0,0,1;3.14159rad)
  Radius = 1.7
FEATURE [Part::Cylinder] Cylinder031
  Angle = 360
  AttacherType = Attacher::AttachEngine3D
  Height = 10
  Placement = pos=(0,15,-5) rot=(0,0,1;1.5708rad)
  Radius = 1.7
FEATURE [Part::Cylinder] Cylinder032
  Angle = 360
  AttacherType = Attacher::AttachEngine3D
  Height = 10
  Placement = pos=(-15,0,-5) rot=(0,0,1;3.14159rad)
  Radius = 1.7
FEATURE [Part::Cylinder] Cylinder033
  Angle = 360
  AttacherType = Attacher::AttachEngine3D
  Height = 10
  Placement = pos=(0,-15,-5) rot=(0,0,1;4.71239rad)
  Radius = 1.7
FEATURE [Part::MultiFuse] Fusion103007
  Shapes = -> [Cylinder029,Sphere087,Sphere084,Sphere086,Sphere088,Cylinder032,Cylinder033,Sphere085,Cylinder031,Cylinder030]
FEATURE [Part::Cut] Cut111  label="Ball Plate with Extra Holes"
  Base = -> Cut110
  Tool = -> Fusion103007
note: 2 file-system paths scrubbed to <path> (originals preserved in the JSON sidecar)
